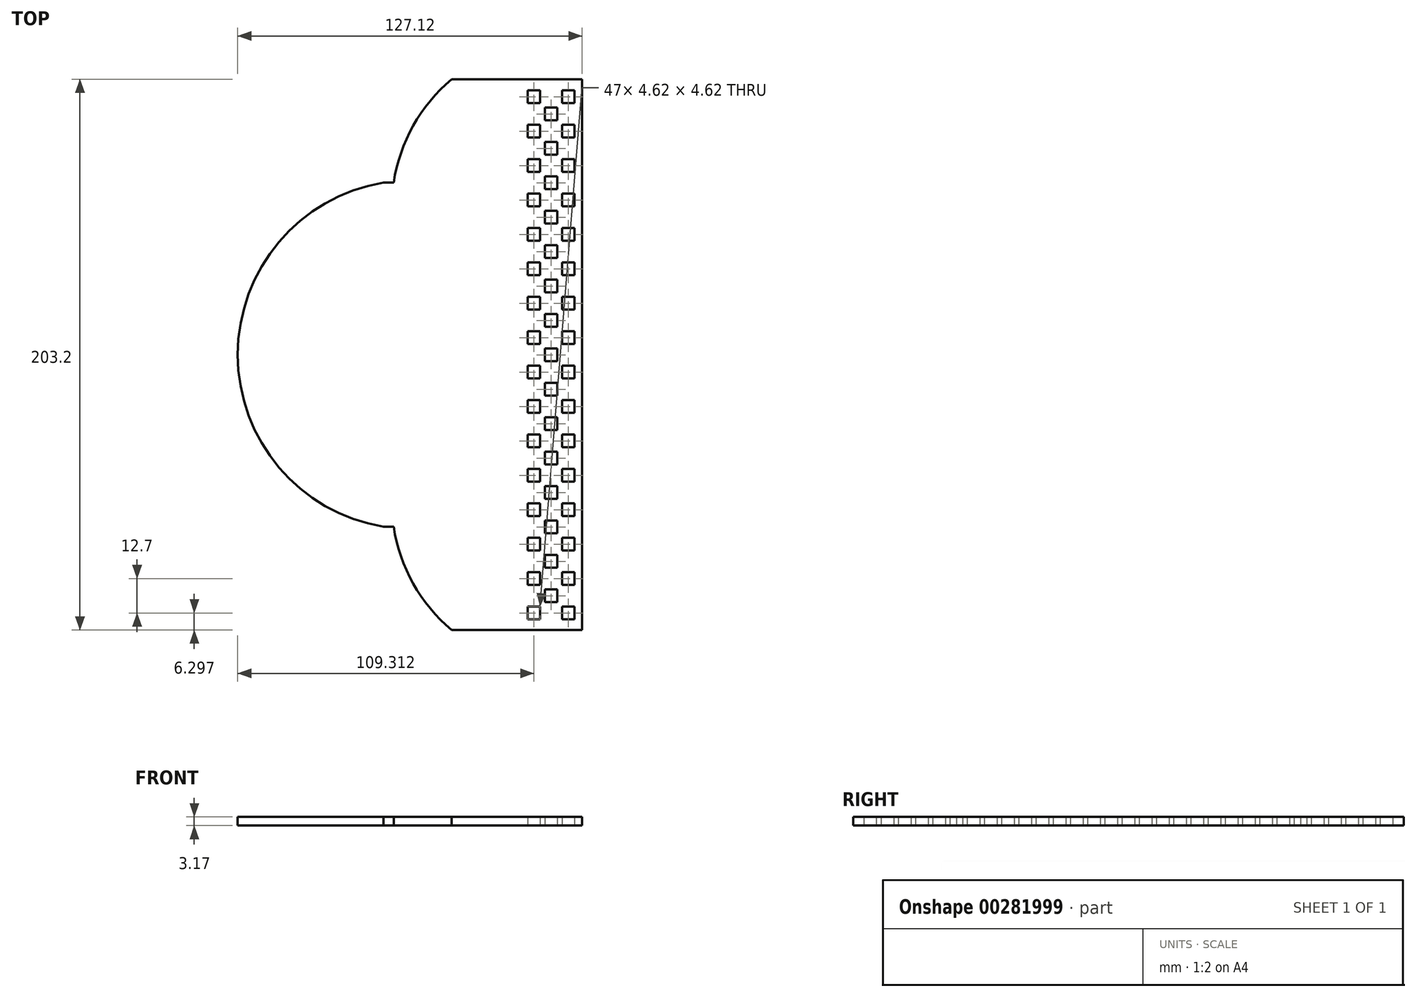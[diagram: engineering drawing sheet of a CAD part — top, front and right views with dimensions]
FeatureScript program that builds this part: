
annotation { "Feature Type Name" : "Feature", "Feature Type Description" : "" }
export const myFeature = defineFeature(function(context is Context, id is Id, definition is map)
    precondition{}
    {
        {
            var Q0;
            Q0=qCreatedBy(makeId("Top.planeOp"),FACE);
            var sketch = newSketch(context, id + "F0", { "sketchPlane" : qUnion([Q0])});
            skLineSegment(sketch, "E0.bottom", {"start": v(-11.58, 137.79) * mm, "end": v(12.55, 137.79) * mm});
            skLineSegment(sketch, "E0.top", {"start": v(-11.58, -65.41) * mm, "end": v(12.55, -65.41) * mm});
            skLineSegment(sketch, "E0.left", {"start": v(-11.58, 137.79) * mm, "end": v(-11.58, -65.41) * mm});
            skLineSegment(sketch, "E0.right", {"start": v(12.55, 137.79) * mm, "end": v(12.55, -65.41) * mm});
            skPoint(sketch, "E1", {"position": v(-7.59, 137.79) * mm});
            skPoint(sketch, "E2", {"position": v(-11.58, 133.7) * mm});
            skLineSegment(sketch, "E3.bottom", {"start": v(-7.59, 133.7) * mm, "end": v(-2.97, 133.7) * mm});
            skLineSegment(sketch, "E3.top", {"start": v(-7.59, 129.08) * mm, "end": v(-2.97, 129.08) * mm});
            skLineSegment(sketch, "E3.left", {"start": v(-7.59, 133.7) * mm, "end": v(-7.59, 129.08) * mm});
            skLineSegment(sketch, "E3.right", {"start": v(-2.97, 133.7) * mm, "end": v(-2.97, 129.08) * mm});
            skPoint(sketch, "E4", {"position": v(-5.28, 133.7) * mm});
            skPoint(sketch, "E5", {"position": v(-7.59, 131.39) * mm});
            skPoint(sketch, "E6", {"position": v(7.42, 133.7) * mm});
            skPoint(sketch, "E7", {"position": v(1.07, 133.7) * mm});
            skLineSegment(sketch, "E8.bottom", {"start": v(5.11, 133.7) * mm, "end": v(9.73, 133.7) * mm});
            skLineSegment(sketch, "E8.top", {"start": v(5.11, 129.08) * mm, "end": v(9.73, 129.08) * mm});
            skLineSegment(sketch, "E8.left", {"start": v(5.11, 133.7) * mm, "end": v(5.11, 129.08) * mm});
            skLineSegment(sketch, "E8.right", {"start": v(9.73, 133.7) * mm, "end": v(9.73, 129.08) * mm});
            skPoint(sketch, "E9", {"position": v(-7.59, 118.84) * mm});
            skPoint(sketch, "E10.0.1.0", {"position": v(7.42, 121) * mm});
            skPoint(sketch, "E10.0.1.1", {"position": v(-7.59, 118.69) * mm});
            skLineSegment(sketch, "E10.0.1.2", {"start": v(9.73, 121) * mm, "end": v(9.73, 116.38) * mm});
            skLineSegment(sketch, "E10.0.1.3", {"start": v(5.11, 121) * mm, "end": v(5.11, 116.38) * mm});
            skLineSegment(sketch, "E10.0.1.4", {"start": v(5.11, 116.38) * mm, "end": v(9.73, 116.38) * mm});
            skLineSegment(sketch, "E10.0.1.5", {"start": v(-2.97, 121) * mm, "end": v(-2.97, 116.38) * mm});
            skLineSegment(sketch, "E10.0.1.6", {"start": v(-7.59, 116.38) * mm, "end": v(-2.97, 116.38) * mm});
            skPoint(sketch, "E10.0.1.7", {"position": v(1.07, 121) * mm});
            skPoint(sketch, "E10.0.1.8", {"position": v(-5.28, 121) * mm});
            skLineSegment(sketch, "E10.0.1.9", {"start": v(5.11, 121) * mm, "end": v(9.73, 121) * mm});
            skLineSegment(sketch, "E10.0.1.10", {"start": v(-7.59, 121) * mm, "end": v(-7.59, 116.38) * mm});
            skLineSegment(sketch, "E10.0.1.11", {"start": v(-7.59, 121) * mm, "end": v(-2.97, 121) * mm});
            skPoint(sketch, "E10.0.2.0", {"position": v(7.42, 108.3) * mm});
            skPoint(sketch, "E10.0.2.1", {"position": v(-7.59, 105.99) * mm});
            skLineSegment(sketch, "E10.0.2.2", {"start": v(9.73, 108.3) * mm, "end": v(9.73, 103.68) * mm});
            skLineSegment(sketch, "E10.0.2.3", {"start": v(5.11, 108.3) * mm, "end": v(5.11, 103.68) * mm});
            skLineSegment(sketch, "E10.0.2.4", {"start": v(5.11, 103.68) * mm, "end": v(9.73, 103.68) * mm});
            skLineSegment(sketch, "E10.0.2.5", {"start": v(-2.97, 108.3) * mm, "end": v(-2.97, 103.68) * mm});
            skLineSegment(sketch, "E10.0.2.6", {"start": v(-7.59, 103.68) * mm, "end": v(-2.97, 103.68) * mm});
            skPoint(sketch, "E10.0.2.7", {"position": v(1.07, 108.3) * mm});
            skPoint(sketch, "E10.0.2.8", {"position": v(-5.28, 108.3) * mm});
            skLineSegment(sketch, "E10.0.2.9", {"start": v(5.11, 108.3) * mm, "end": v(9.73, 108.3) * mm});
            skLineSegment(sketch, "E10.0.2.10", {"start": v(-7.59, 108.3) * mm, "end": v(-7.59, 103.68) * mm});
            skLineSegment(sketch, "E10.0.2.11", {"start": v(-7.59, 108.3) * mm, "end": v(-2.97, 108.3) * mm});
            skPoint(sketch, "E10.0.3.0", {"position": v(7.42, 95.6) * mm});
            skPoint(sketch, "E10.0.3.1", {"position": v(-7.59, 93.29) * mm});
            skLineSegment(sketch, "E10.0.3.2", {"start": v(9.73, 95.6) * mm, "end": v(9.73, 90.98) * mm});
            skLineSegment(sketch, "E10.0.3.3", {"start": v(5.11, 95.6) * mm, "end": v(5.11, 90.98) * mm});
            skLineSegment(sketch, "E10.0.3.4", {"start": v(5.11, 90.98) * mm, "end": v(9.73, 90.98) * mm});
            skLineSegment(sketch, "E10.0.3.5", {"start": v(-2.97, 95.6) * mm, "end": v(-2.97, 90.98) * mm});
            skLineSegment(sketch, "E10.0.3.6", {"start": v(-7.59, 90.98) * mm, "end": v(-2.97, 90.98) * mm});
            skPoint(sketch, "E10.0.3.7", {"position": v(1.07, 95.6) * mm});
            skPoint(sketch, "E10.0.3.8", {"position": v(-5.28, 95.6) * mm});
            skLineSegment(sketch, "E10.0.3.9", {"start": v(5.11, 95.6) * mm, "end": v(9.73, 95.6) * mm});
            skLineSegment(sketch, "E10.0.3.10", {"start": v(-7.59, 95.6) * mm, "end": v(-7.59, 90.98) * mm});
            skLineSegment(sketch, "E10.0.3.11", {"start": v(-7.59, 95.6) * mm, "end": v(-2.97, 95.6) * mm});
            skPoint(sketch, "E10.0.4.0", {"position": v(7.42, 82.9) * mm});
            skPoint(sketch, "E10.0.4.1", {"position": v(-7.59, 80.59) * mm});
            skLineSegment(sketch, "E10.0.4.2", {"start": v(9.73, 82.9) * mm, "end": v(9.73, 78.28) * mm});
            skLineSegment(sketch, "E10.0.4.3", {"start": v(5.11, 82.9) * mm, "end": v(5.11, 78.28) * mm});
            skLineSegment(sketch, "E10.0.4.4", {"start": v(5.11, 78.28) * mm, "end": v(9.73, 78.28) * mm});
            skLineSegment(sketch, "E10.0.4.5", {"start": v(-2.97, 82.9) * mm, "end": v(-2.97, 78.28) * mm});
            skLineSegment(sketch, "E10.0.4.6", {"start": v(-7.59, 78.28) * mm, "end": v(-2.97, 78.28) * mm});
            skPoint(sketch, "E10.0.4.7", {"position": v(1.07, 82.9) * mm});
            skPoint(sketch, "E10.0.4.8", {"position": v(-5.28, 82.9) * mm});
            skLineSegment(sketch, "E10.0.4.9", {"start": v(5.11, 82.9) * mm, "end": v(9.73, 82.9) * mm});
            skLineSegment(sketch, "E10.0.4.10", {"start": v(-7.59, 82.9) * mm, "end": v(-7.59, 78.28) * mm});
            skLineSegment(sketch, "E10.0.4.11", {"start": v(-7.59, 82.9) * mm, "end": v(-2.97, 82.9) * mm});
            skPoint(sketch, "E10.0.5.0", {"position": v(7.42, 70.2) * mm});
            skPoint(sketch, "E10.0.5.1", {"position": v(-7.59, 67.89) * mm});
            skLineSegment(sketch, "E10.0.5.2", {"start": v(9.73, 70.2) * mm, "end": v(9.73, 65.58) * mm});
            skLineSegment(sketch, "E10.0.5.3", {"start": v(5.11, 70.2) * mm, "end": v(5.11, 65.58) * mm});
            skLineSegment(sketch, "E10.0.5.4", {"start": v(5.11, 65.58) * mm, "end": v(9.73, 65.58) * mm});
            skLineSegment(sketch, "E10.0.5.5", {"start": v(-2.97, 70.2) * mm, "end": v(-2.97, 65.58) * mm});
            skLineSegment(sketch, "E10.0.5.6", {"start": v(-7.59, 65.58) * mm, "end": v(-2.97, 65.58) * mm});
            skPoint(sketch, "E10.0.5.7", {"position": v(1.07, 70.2) * mm});
            skPoint(sketch, "E10.0.5.8", {"position": v(-5.28, 70.2) * mm});
            skLineSegment(sketch, "E10.0.5.9", {"start": v(5.11, 70.2) * mm, "end": v(9.73, 70.2) * mm});
            skLineSegment(sketch, "E10.0.5.10", {"start": v(-7.59, 70.2) * mm, "end": v(-7.59, 65.58) * mm});
            skLineSegment(sketch, "E10.0.5.11", {"start": v(-7.59, 70.2) * mm, "end": v(-2.97, 70.2) * mm});
            skPoint(sketch, "E10.0.6.0", {"position": v(7.42, 57.5) * mm});
            skPoint(sketch, "E10.0.6.1", {"position": v(-7.59, 55.19) * mm});
            skLineSegment(sketch, "E10.0.6.2", {"start": v(9.73, 57.5) * mm, "end": v(9.73, 52.88) * mm});
            skLineSegment(sketch, "E10.0.6.3", {"start": v(5.11, 57.5) * mm, "end": v(5.11, 52.88) * mm});
            skLineSegment(sketch, "E10.0.6.4", {"start": v(5.11, 52.88) * mm, "end": v(9.73, 52.88) * mm});
            skLineSegment(sketch, "E10.0.6.5", {"start": v(-2.97, 57.5) * mm, "end": v(-2.97, 52.88) * mm});
            skLineSegment(sketch, "E10.0.6.6", {"start": v(-7.59, 52.88) * mm, "end": v(-2.97, 52.88) * mm});
            skPoint(sketch, "E10.0.6.7", {"position": v(1.07, 57.5) * mm});
            skPoint(sketch, "E10.0.6.8", {"position": v(-5.28, 57.5) * mm});
            skLineSegment(sketch, "E10.0.6.9", {"start": v(5.11, 57.5) * mm, "end": v(9.73, 57.5) * mm});
            skLineSegment(sketch, "E10.0.6.10", {"start": v(-7.59, 57.5) * mm, "end": v(-7.59, 52.88) * mm});
            skLineSegment(sketch, "E10.0.6.11", {"start": v(-7.59, 57.5) * mm, "end": v(-2.97, 57.5) * mm});
            skPoint(sketch, "E10.0.7.0", {"position": v(7.42, 44.8) * mm});
            skPoint(sketch, "E10.0.7.1", {"position": v(-7.59, 42.49) * mm});
            skLineSegment(sketch, "E10.0.7.2", {"start": v(9.73, 44.8) * mm, "end": v(9.73, 40.18) * mm});
            skLineSegment(sketch, "E10.0.7.3", {"start": v(5.11, 44.8) * mm, "end": v(5.11, 40.18) * mm});
            skLineSegment(sketch, "E10.0.7.4", {"start": v(5.11, 40.18) * mm, "end": v(9.73, 40.18) * mm});
            skLineSegment(sketch, "E10.0.7.5", {"start": v(-2.97, 44.8) * mm, "end": v(-2.97, 40.18) * mm});
            skLineSegment(sketch, "E10.0.7.6", {"start": v(-7.59, 40.18) * mm, "end": v(-2.97, 40.18) * mm});
            skPoint(sketch, "E10.0.7.7", {"position": v(1.07, 44.8) * mm});
            skPoint(sketch, "E10.0.7.8", {"position": v(-5.28, 44.8) * mm});
            skLineSegment(sketch, "E10.0.7.9", {"start": v(5.11, 44.8) * mm, "end": v(9.73, 44.8) * mm});
            skLineSegment(sketch, "E10.0.7.10", {"start": v(-7.59, 44.8) * mm, "end": v(-7.59, 40.18) * mm});
            skLineSegment(sketch, "E10.0.7.11", {"start": v(-7.59, 44.8) * mm, "end": v(-2.97, 44.8) * mm});
            skPoint(sketch, "E10.0.8.0", {"position": v(7.42, 32.1) * mm});
            skPoint(sketch, "E10.0.8.1", {"position": v(-7.59, 29.79) * mm});
            skLineSegment(sketch, "E10.0.8.2", {"start": v(9.73, 32.1) * mm, "end": v(9.73, 27.48) * mm});
            skLineSegment(sketch, "E10.0.8.3", {"start": v(5.11, 32.1) * mm, "end": v(5.11, 27.48) * mm});
            skLineSegment(sketch, "E10.0.8.4", {"start": v(5.11, 27.48) * mm, "end": v(9.73, 27.48) * mm});
            skLineSegment(sketch, "E10.0.8.5", {"start": v(-2.97, 32.1) * mm, "end": v(-2.97, 27.48) * mm});
            skLineSegment(sketch, "E10.0.8.6", {"start": v(-7.59, 27.48) * mm, "end": v(-2.97, 27.48) * mm});
            skPoint(sketch, "E10.0.8.7", {"position": v(1.07, 32.1) * mm});
            skPoint(sketch, "E10.0.8.8", {"position": v(-5.28, 32.1) * mm});
            skLineSegment(sketch, "E10.0.8.9", {"start": v(5.11, 32.1) * mm, "end": v(9.73, 32.1) * mm});
            skLineSegment(sketch, "E10.0.8.10", {"start": v(-7.59, 32.1) * mm, "end": v(-7.59, 27.48) * mm});
            skLineSegment(sketch, "E10.0.8.11", {"start": v(-7.59, 32.1) * mm, "end": v(-2.97, 32.1) * mm});
            skPoint(sketch, "E10.0.9.0", {"position": v(7.42, 19.4) * mm});
            skPoint(sketch, "E10.0.9.1", {"position": v(-7.59, 17.09) * mm});
            skLineSegment(sketch, "E10.0.9.2", {"start": v(9.73, 19.4) * mm, "end": v(9.73, 14.78) * mm});
            skLineSegment(sketch, "E10.0.9.3", {"start": v(5.11, 19.4) * mm, "end": v(5.11, 14.78) * mm});
            skLineSegment(sketch, "E10.0.9.4", {"start": v(5.11, 14.78) * mm, "end": v(9.73, 14.78) * mm});
            skLineSegment(sketch, "E10.0.9.5", {"start": v(-2.97, 19.4) * mm, "end": v(-2.97, 14.78) * mm});
            skLineSegment(sketch, "E10.0.9.6", {"start": v(-7.59, 14.78) * mm, "end": v(-2.97, 14.78) * mm});
            skPoint(sketch, "E10.0.9.7", {"position": v(1.07, 19.4) * mm});
            skPoint(sketch, "E10.0.9.8", {"position": v(-5.28, 19.4) * mm});
            skLineSegment(sketch, "E10.0.9.9", {"start": v(5.11, 19.4) * mm, "end": v(9.73, 19.4) * mm});
            skLineSegment(sketch, "E10.0.9.10", {"start": v(-7.59, 19.4) * mm, "end": v(-7.59, 14.78) * mm});
            skLineSegment(sketch, "E10.0.9.11", {"start": v(-7.59, 19.4) * mm, "end": v(-2.97, 19.4) * mm});
            skPoint(sketch, "E10.0.10.0", {"position": v(7.42, 6.7) * mm});
            skPoint(sketch, "E10.0.10.1", {"position": v(-7.59, 4.39) * mm});
            skLineSegment(sketch, "E10.0.10.2", {"start": v(9.73, 6.7) * mm, "end": v(9.73, 2.08) * mm});
            skLineSegment(sketch, "E10.0.10.3", {"start": v(5.11, 6.7) * mm, "end": v(5.11, 2.08) * mm});
            skLineSegment(sketch, "E10.0.10.4", {"start": v(5.11, 2.08) * mm, "end": v(9.73, 2.08) * mm});
            skLineSegment(sketch, "E10.0.10.5", {"start": v(-2.97, 6.7) * mm, "end": v(-2.97, 2.08) * mm});
            skLineSegment(sketch, "E10.0.10.6", {"start": v(-7.59, 2.08) * mm, "end": v(-2.97, 2.08) * mm});
            skPoint(sketch, "E10.0.10.7", {"position": v(1.07, 6.7) * mm});
            skPoint(sketch, "E10.0.10.8", {"position": v(-5.28, 6.7) * mm});
            skLineSegment(sketch, "E10.0.10.9", {"start": v(5.11, 6.7) * mm, "end": v(9.73, 6.7) * mm});
            skLineSegment(sketch, "E10.0.10.10", {"start": v(-7.59, 6.7) * mm, "end": v(-7.59, 2.08) * mm});
            skLineSegment(sketch, "E10.0.10.11", {"start": v(-7.59, 6.7) * mm, "end": v(-2.97, 6.7) * mm});
            skPoint(sketch, "E10.0.11.0", {"position": v(7.42, -6) * mm});
            skPoint(sketch, "E10.0.11.1", {"position": v(-7.59, -8.31) * mm});
            skLineSegment(sketch, "E10.0.11.2", {"start": v(9.73, -6) * mm, "end": v(9.73, -10.62) * mm});
            skLineSegment(sketch, "E10.0.11.3", {"start": v(5.11, -6) * mm, "end": v(5.11, -10.62) * mm});
            skLineSegment(sketch, "E10.0.11.4", {"start": v(5.11, -10.62) * mm, "end": v(9.73, -10.62) * mm});
            skLineSegment(sketch, "E10.0.11.5", {"start": v(-2.97, -6) * mm, "end": v(-2.97, -10.62) * mm});
            skLineSegment(sketch, "E10.0.11.6", {"start": v(-7.59, -10.62) * mm, "end": v(-2.97, -10.62) * mm});
            skPoint(sketch, "E10.0.11.7", {"position": v(1.07, -6) * mm});
            skPoint(sketch, "E10.0.11.8", {"position": v(-5.28, -6) * mm});
            skLineSegment(sketch, "E10.0.11.9", {"start": v(5.11, -6) * mm, "end": v(9.73, -6) * mm});
            skLineSegment(sketch, "E10.0.11.10", {"start": v(-7.59, -6) * mm, "end": v(-7.59, -10.62) * mm});
            skLineSegment(sketch, "E10.0.11.11", {"start": v(-7.59, -6) * mm, "end": v(-2.97, -6) * mm});
            skPoint(sketch, "E10.0.12.0", {"position": v(7.42, -18.7) * mm});
            skPoint(sketch, "E10.0.12.1", {"position": v(-7.59, -21.01) * mm});
            skLineSegment(sketch, "E10.0.12.2", {"start": v(9.73, -18.7) * mm, "end": v(9.73, -23.32) * mm});
            skLineSegment(sketch, "E10.0.12.3", {"start": v(5.11, -18.7) * mm, "end": v(5.11, -23.32) * mm});
            skLineSegment(sketch, "E10.0.12.4", {"start": v(5.11, -23.32) * mm, "end": v(9.73, -23.32) * mm});
            skLineSegment(sketch, "E10.0.12.5", {"start": v(-2.97, -18.7) * mm, "end": v(-2.97, -23.32) * mm});
            skLineSegment(sketch, "E10.0.12.6", {"start": v(-7.59, -23.32) * mm, "end": v(-2.97, -23.32) * mm});
            skPoint(sketch, "E10.0.12.7", {"position": v(1.07, -18.7) * mm});
            skPoint(sketch, "E10.0.12.8", {"position": v(-5.28, -18.7) * mm});
            skLineSegment(sketch, "E10.0.12.9", {"start": v(5.11, -18.7) * mm, "end": v(9.73, -18.7) * mm});
            skLineSegment(sketch, "E10.0.12.10", {"start": v(-7.59, -18.7) * mm, "end": v(-7.59, -23.32) * mm});
            skLineSegment(sketch, "E10.0.12.11", {"start": v(-7.59, -18.7) * mm, "end": v(-2.97, -18.7) * mm});
            skPoint(sketch, "E10.0.13.0", {"position": v(7.42, -31.4) * mm});
            skPoint(sketch, "E10.0.13.1", {"position": v(-7.59, -33.71) * mm});
            skLineSegment(sketch, "E10.0.13.2", {"start": v(9.73, -31.4) * mm, "end": v(9.73, -36.02) * mm});
            skLineSegment(sketch, "E10.0.13.3", {"start": v(5.11, -31.4) * mm, "end": v(5.11, -36.02) * mm});
            skLineSegment(sketch, "E10.0.13.4", {"start": v(5.11, -36.02) * mm, "end": v(9.73, -36.02) * mm});
            skLineSegment(sketch, "E10.0.13.5", {"start": v(-2.97, -31.4) * mm, "end": v(-2.97, -36.02) * mm});
            skLineSegment(sketch, "E10.0.13.6", {"start": v(-7.59, -36.02) * mm, "end": v(-2.97, -36.02) * mm});
            skPoint(sketch, "E10.0.13.7", {"position": v(1.07, -31.4) * mm});
            skPoint(sketch, "E10.0.13.8", {"position": v(-5.28, -31.4) * mm});
            skLineSegment(sketch, "E10.0.13.9", {"start": v(5.11, -31.4) * mm, "end": v(9.73, -31.4) * mm});
            skLineSegment(sketch, "E10.0.13.10", {"start": v(-7.59, -31.4) * mm, "end": v(-7.59, -36.02) * mm});
            skLineSegment(sketch, "E10.0.13.11", {"start": v(-7.59, -31.4) * mm, "end": v(-2.97, -31.4) * mm});
            skPoint(sketch, "E10.0.14.0", {"position": v(7.42, -44.1) * mm});
            skPoint(sketch, "E10.0.14.1", {"position": v(-7.59, -46.41) * mm});
            skLineSegment(sketch, "E10.0.14.2", {"start": v(9.73, -44.1) * mm, "end": v(9.73, -48.72) * mm});
            skLineSegment(sketch, "E10.0.14.3", {"start": v(5.11, -44.1) * mm, "end": v(5.11, -48.72) * mm});
            skLineSegment(sketch, "E10.0.14.4", {"start": v(5.11, -48.72) * mm, "end": v(9.73, -48.72) * mm});
            skLineSegment(sketch, "E10.0.14.5", {"start": v(-2.97, -44.1) * mm, "end": v(-2.97, -48.72) * mm});
            skLineSegment(sketch, "E10.0.14.6", {"start": v(-7.59, -48.72) * mm, "end": v(-2.97, -48.72) * mm});
            skPoint(sketch, "E10.0.14.7", {"position": v(1.07, -44.1) * mm});
            skPoint(sketch, "E10.0.14.8", {"position": v(-5.28, -44.1) * mm});
            skLineSegment(sketch, "E10.0.14.9", {"start": v(5.11, -44.1) * mm, "end": v(9.73, -44.1) * mm});
            skLineSegment(sketch, "E10.0.14.10", {"start": v(-7.59, -44.1) * mm, "end": v(-7.59, -48.72) * mm});
            skLineSegment(sketch, "E10.0.14.11", {"start": v(-7.59, -44.1) * mm, "end": v(-2.97, -44.1) * mm});
            skPoint(sketch, "E10.0.15.0", {"position": v(7.42, -56.8) * mm});
            skPoint(sketch, "E10.0.15.1", {"position": v(-7.59, -59.11) * mm});
            skLineSegment(sketch, "E10.0.15.2", {"start": v(9.73, -56.8) * mm, "end": v(9.73, -61.42) * mm});
            skLineSegment(sketch, "E10.0.15.3", {"start": v(5.11, -56.8) * mm, "end": v(5.11, -61.42) * mm});
            skLineSegment(sketch, "E10.0.15.4", {"start": v(5.11, -61.42) * mm, "end": v(9.73, -61.42) * mm});
            skLineSegment(sketch, "E10.0.15.5", {"start": v(-2.97, -56.8) * mm, "end": v(-2.97, -61.42) * mm});
            skLineSegment(sketch, "E10.0.15.6", {"start": v(-7.59, -61.42) * mm, "end": v(-2.97, -61.42) * mm});
            skPoint(sketch, "E10.0.15.7", {"position": v(1.07, -56.8) * mm});
            skPoint(sketch, "E10.0.15.8", {"position": v(-5.28, -56.8) * mm});
            skLineSegment(sketch, "E10.0.15.9", {"start": v(5.11, -56.8) * mm, "end": v(9.73, -56.8) * mm});
            skLineSegment(sketch, "E10.0.15.10", {"start": v(-7.59, -56.8) * mm, "end": v(-7.59, -61.42) * mm});
            skLineSegment(sketch, "E10.0.15.11", {"start": v(-7.59, -56.8) * mm, "end": v(-2.97, -56.8) * mm});
            skLineSegment(sketch, "E10.direction1", {"start": v(-7.59, 131.39) * mm, "end": v(17.81, 131.39) * mm, "construction": true});
            skLineSegment(sketch, "E10.direction2", {"start": v(-7.59, 131.39) * mm, "end": v(-7.59, 118.69) * mm, "construction": true});
            skPoint(sketch, "E11", {"position": v(1.07, 127.35) * mm});
            skLineSegment(sketch, "E12.bottom", {"start": v(-1.24, 127.35) * mm, "end": v(3.38, 127.35) * mm});
            skLineSegment(sketch, "E12.top", {"start": v(-1.24, 122.73) * mm, "end": v(3.38, 122.73) * mm});
            skLineSegment(sketch, "E12.left", {"start": v(-1.24, 127.35) * mm, "end": v(-1.24, 122.73) * mm});
            skLineSegment(sketch, "E12.right", {"start": v(3.38, 127.35) * mm, "end": v(3.38, 122.73) * mm});
            skLineSegment(sketch, "E13.0.1.0", {"start": v(3.38, 114.65) * mm, "end": v(3.38, 110.03) * mm});
            skLineSegment(sketch, "E13.0.1.1", {"start": v(-1.24, 114.65) * mm, "end": v(-1.24, 110.03) * mm});
            skLineSegment(sketch, "E13.0.1.2", {"start": v(-1.24, 110.03) * mm, "end": v(3.38, 110.03) * mm});
            skPoint(sketch, "E13.0.1.3", {"position": v(1.07, 114.65) * mm});
            skLineSegment(sketch, "E13.0.1.4", {"start": v(-1.24, 114.65) * mm, "end": v(3.38, 114.65) * mm});
            skLineSegment(sketch, "E13.0.2.0", {"start": v(3.38, 101.95) * mm, "end": v(3.38, 97.33) * mm});
            skLineSegment(sketch, "E13.0.2.1", {"start": v(-1.24, 101.95) * mm, "end": v(-1.24, 97.33) * mm});
            skLineSegment(sketch, "E13.0.2.2", {"start": v(-1.24, 97.33) * mm, "end": v(3.38, 97.33) * mm});
            skPoint(sketch, "E13.0.2.3", {"position": v(1.07, 101.95) * mm});
            skLineSegment(sketch, "E13.0.2.4", {"start": v(-1.24, 101.95) * mm, "end": v(3.38, 101.95) * mm});
            skLineSegment(sketch, "E13.0.3.0", {"start": v(3.38, 89.25) * mm, "end": v(3.38, 84.63) * mm});
            skLineSegment(sketch, "E13.0.3.1", {"start": v(-1.24, 89.25) * mm, "end": v(-1.24, 84.63) * mm});
            skLineSegment(sketch, "E13.0.3.2", {"start": v(-1.24, 84.63) * mm, "end": v(3.38, 84.63) * mm});
            skPoint(sketch, "E13.0.3.3", {"position": v(1.07, 89.25) * mm});
            skLineSegment(sketch, "E13.0.3.4", {"start": v(-1.24, 89.25) * mm, "end": v(3.38, 89.25) * mm});
            skLineSegment(sketch, "E13.0.4.0", {"start": v(3.38, 76.55) * mm, "end": v(3.38, 71.93) * mm});
            skLineSegment(sketch, "E13.0.4.1", {"start": v(-1.24, 76.55) * mm, "end": v(-1.24, 71.93) * mm});
            skLineSegment(sketch, "E13.0.4.2", {"start": v(-1.24, 71.93) * mm, "end": v(3.38, 71.93) * mm});
            skPoint(sketch, "E13.0.4.3", {"position": v(1.07, 76.55) * mm});
            skLineSegment(sketch, "E13.0.4.4", {"start": v(-1.24, 76.55) * mm, "end": v(3.38, 76.55) * mm});
            skLineSegment(sketch, "E13.0.5.0", {"start": v(3.38, 63.85) * mm, "end": v(3.38, 59.23) * mm});
            skLineSegment(sketch, "E13.0.5.1", {"start": v(-1.24, 63.85) * mm, "end": v(-1.24, 59.23) * mm});
            skLineSegment(sketch, "E13.0.5.2", {"start": v(-1.24, 59.23) * mm, "end": v(3.38, 59.23) * mm});
            skPoint(sketch, "E13.0.5.3", {"position": v(1.07, 63.85) * mm});
            skLineSegment(sketch, "E13.0.5.4", {"start": v(-1.24, 63.85) * mm, "end": v(3.38, 63.85) * mm});
            skLineSegment(sketch, "E13.0.6.0", {"start": v(3.38, 51.15) * mm, "end": v(3.38, 46.53) * mm});
            skLineSegment(sketch, "E13.0.6.1", {"start": v(-1.24, 51.15) * mm, "end": v(-1.24, 46.53) * mm});
            skLineSegment(sketch, "E13.0.6.2", {"start": v(-1.24, 46.53) * mm, "end": v(3.38, 46.53) * mm});
            skPoint(sketch, "E13.0.6.3", {"position": v(1.07, 51.15) * mm});
            skLineSegment(sketch, "E13.0.6.4", {"start": v(-1.24, 51.15) * mm, "end": v(3.38, 51.15) * mm});
            skLineSegment(sketch, "E13.0.7.0", {"start": v(3.38, 38.45) * mm, "end": v(3.38, 33.83) * mm});
            skLineSegment(sketch, "E13.0.7.1", {"start": v(-1.24, 38.45) * mm, "end": v(-1.24, 33.83) * mm});
            skLineSegment(sketch, "E13.0.7.2", {"start": v(-1.24, 33.83) * mm, "end": v(3.38, 33.83) * mm});
            skPoint(sketch, "E13.0.7.3", {"position": v(1.07, 38.45) * mm});
            skLineSegment(sketch, "E13.0.7.4", {"start": v(-1.24, 38.45) * mm, "end": v(3.38, 38.45) * mm});
            skLineSegment(sketch, "E13.0.8.0", {"start": v(3.38, 25.75) * mm, "end": v(3.38, 21.13) * mm});
            skLineSegment(sketch, "E13.0.8.1", {"start": v(-1.24, 25.75) * mm, "end": v(-1.24, 21.13) * mm});
            skLineSegment(sketch, "E13.0.8.2", {"start": v(-1.24, 21.13) * mm, "end": v(3.38, 21.13) * mm});
            skPoint(sketch, "E13.0.8.3", {"position": v(1.07, 25.75) * mm});
            skLineSegment(sketch, "E13.0.8.4", {"start": v(-1.24, 25.75) * mm, "end": v(3.38, 25.75) * mm});
            skLineSegment(sketch, "E13.0.9.0", {"start": v(3.38, 13.05) * mm, "end": v(3.38, 8.43) * mm});
            skLineSegment(sketch, "E13.0.9.1", {"start": v(-1.24, 13.05) * mm, "end": v(-1.24, 8.43) * mm});
            skLineSegment(sketch, "E13.0.9.2", {"start": v(-1.24, 8.43) * mm, "end": v(3.38, 8.43) * mm});
            skPoint(sketch, "E13.0.9.3", {"position": v(1.07, 13.05) * mm});
            skLineSegment(sketch, "E13.0.9.4", {"start": v(-1.24, 13.05) * mm, "end": v(3.38, 13.05) * mm});
            skLineSegment(sketch, "E13.0.10.0", {"start": v(3.38, 0.35) * mm, "end": v(3.38, -4.27) * mm});
            skLineSegment(sketch, "E13.0.10.1", {"start": v(-1.24, 0.35) * mm, "end": v(-1.24, -4.27) * mm});
            skLineSegment(sketch, "E13.0.10.2", {"start": v(-1.24, -4.27) * mm, "end": v(3.38, -4.27) * mm});
            skPoint(sketch, "E13.0.10.3", {"position": v(1.07, 0.35) * mm});
            skLineSegment(sketch, "E13.0.10.4", {"start": v(-1.24, 0.35) * mm, "end": v(3.38, 0.35) * mm});
            skLineSegment(sketch, "E13.0.11.0", {"start": v(3.38, -12.35) * mm, "end": v(3.38, -16.97) * mm});
            skLineSegment(sketch, "E13.0.11.1", {"start": v(-1.24, -12.35) * mm, "end": v(-1.24, -16.97) * mm});
            skLineSegment(sketch, "E13.0.11.2", {"start": v(-1.24, -16.97) * mm, "end": v(3.38, -16.97) * mm});
            skPoint(sketch, "E13.0.11.3", {"position": v(1.07, -12.35) * mm});
            skLineSegment(sketch, "E13.0.11.4", {"start": v(-1.24, -12.35) * mm, "end": v(3.38, -12.35) * mm});
            skLineSegment(sketch, "E13.0.12.0", {"start": v(3.38, -25.05) * mm, "end": v(3.38, -29.67) * mm});
            skLineSegment(sketch, "E13.0.12.1", {"start": v(-1.24, -25.05) * mm, "end": v(-1.24, -29.67) * mm});
            skLineSegment(sketch, "E13.0.12.2", {"start": v(-1.24, -29.67) * mm, "end": v(3.38, -29.67) * mm});
            skPoint(sketch, "E13.0.12.3", {"position": v(1.07, -25.05) * mm});
            skLineSegment(sketch, "E13.0.12.4", {"start": v(-1.24, -25.05) * mm, "end": v(3.38, -25.05) * mm});
            skLineSegment(sketch, "E13.0.13.0", {"start": v(3.38, -37.75) * mm, "end": v(3.38, -42.37) * mm});
            skLineSegment(sketch, "E13.0.13.1", {"start": v(-1.24, -37.75) * mm, "end": v(-1.24, -42.37) * mm});
            skLineSegment(sketch, "E13.0.13.2", {"start": v(-1.24, -42.37) * mm, "end": v(3.38, -42.37) * mm});
            skPoint(sketch, "E13.0.13.3", {"position": v(1.07, -37.75) * mm});
            skLineSegment(sketch, "E13.0.13.4", {"start": v(-1.24, -37.75) * mm, "end": v(3.38, -37.75) * mm});
            skLineSegment(sketch, "E13.0.14.0", {"start": v(3.38, -50.45) * mm, "end": v(3.38, -55.07) * mm});
            skLineSegment(sketch, "E13.0.14.1", {"start": v(-1.24, -50.45) * mm, "end": v(-1.24, -55.07) * mm});
            skLineSegment(sketch, "E13.0.14.2", {"start": v(-1.24, -55.07) * mm, "end": v(3.38, -55.07) * mm});
            skPoint(sketch, "E13.0.14.3", {"position": v(1.07, -50.45) * mm});
            skLineSegment(sketch, "E13.0.14.4", {"start": v(-1.24, -50.45) * mm, "end": v(3.38, -50.45) * mm});
            skLineSegment(sketch, "E13.direction1", {"start": v(-1.24, 122.73) * mm, "end": v(24.16, 122.73) * mm, "construction": true});
            skLineSegment(sketch, "E13.direction2", {"start": v(-1.24, 122.73) * mm, "end": v(-1.24, 110.03) * mm, "construction": true});
            skSolve(sketch);
        }
        {
            var Q0;
            Q0=makeQuery(id+"F0.imprint","IMPRINT",FACE,{"disambiguationData":[TD([[makeQuery(id+"F0.imprint","IMPRINT",EDGE,{"derivedFrom":sQuery(id+"F0.wireOp",EDGE,"E0.bottom")}),-1.0]])]});
            extrude(context, id + "F1", {"entities" : qUnion([Q0]), "depth" : 3.17 * mm});
        }
        {
            var Q0;
            Q0=makeQuery(id+"F1.opExtrude","SWEPT_BODY",BODY,{"disambiguationData":[OSD([sQuery(id+"F0.wireOp",EDGE,"E0.bottom"),sQuery(id+"F0.wireOp",EDGE,"E0.top"),sQuery(id+"F0.wireOp",EDGE,"E0.left"),sQuery(id+"F0.wireOp",EDGE,"E0.right"),sQuery(id+"F0.wireOp",EDGE,"E3.bottom"),sQuery(id+"F0.wireOp",EDGE,"E3.top"),sQuery(id+"F0.wireOp",EDGE,"E3.left"),sQuery(id+"F0.wireOp",EDGE,"E3.right"),sQuery(id+"F0.wireOp",EDGE,"E8.bottom"),sQuery(id+"F0.wireOp",EDGE,"E8.top"),sQuery(id+"F0.wireOp",EDGE,"E8.left"),sQuery(id+"F0.wireOp",EDGE,"E8.right"),sQuery(id+"F0.wireOp",EDGE,"E10.0.1.2"),sQuery(id+"F0.wireOp",EDGE,"E10.0.1.3"),sQuery(id+"F0.wireOp",EDGE,"E10.0.1.4"),sQuery(id+"F0.wireOp",EDGE,"E10.0.1.5"),sQuery(id+"F0.wireOp",EDGE,"E10.0.1.6"),sQuery(id+"F0.wireOp",EDGE,"E10.0.1.9"),sQuery(id+"F0.wireOp",EDGE,"E10.0.1.10"),sQuery(id+"F0.wireOp",EDGE,"E10.0.1.11"),sQuery(id+"F0.wireOp",EDGE,"E10.0.2.2"),sQuery(id+"F0.wireOp",EDGE,"E10.0.2.3"),sQuery(id+"F0.wireOp",EDGE,"E10.0.2.4"),sQuery(id+"F0.wireOp",EDGE,"E10.0.2.5"),sQuery(id+"F0.wireOp",EDGE,"E10.0.2.6"),sQuery(id+"F0.wireOp",EDGE,"E10.0.2.9"),sQuery(id+"F0.wireOp",EDGE,"E10.0.2.10"),sQuery(id+"F0.wireOp",EDGE,"E10.0.2.11"),sQuery(id+"F0.wireOp",EDGE,"E10.0.3.2"),sQuery(id+"F0.wireOp",EDGE,"E10.0.3.3"),sQuery(id+"F0.wireOp",EDGE,"E10.0.3.4"),sQuery(id+"F0.wireOp",EDGE,"E10.0.3.5"),sQuery(id+"F0.wireOp",EDGE,"E10.0.3.6"),sQuery(id+"F0.wireOp",EDGE,"E10.0.3.9"),sQuery(id+"F0.wireOp",EDGE,"E10.0.3.10"),sQuery(id+"F0.wireOp",EDGE,"E10.0.3.11"),sQuery(id+"F0.wireOp",EDGE,"E10.0.4.2"),sQuery(id+"F0.wireOp",EDGE,"E10.0.4.3"),sQuery(id+"F0.wireOp",EDGE,"E10.0.4.4"),sQuery(id+"F0.wireOp",EDGE,"E10.0.4.5"),sQuery(id+"F0.wireOp",EDGE,"E10.0.4.6"),sQuery(id+"F0.wireOp",EDGE,"E10.0.4.9"),sQuery(id+"F0.wireOp",EDGE,"E10.0.4.10"),sQuery(id+"F0.wireOp",EDGE,"E10.0.4.11"),sQuery(id+"F0.wireOp",EDGE,"E10.0.5.2"),sQuery(id+"F0.wireOp",EDGE,"E10.0.5.3"),sQuery(id+"F0.wireOp",EDGE,"E10.0.5.4"),sQuery(id+"F0.wireOp",EDGE,"E10.0.5.5"),sQuery(id+"F0.wireOp",EDGE,"E10.0.5.6"),sQuery(id+"F0.wireOp",EDGE,"E10.0.5.9"),sQuery(id+"F0.wireOp",EDGE,"E10.0.5.10"),sQuery(id+"F0.wireOp",EDGE,"E10.0.5.11"),sQuery(id+"F0.wireOp",EDGE,"E10.0.6.2"),sQuery(id+"F0.wireOp",EDGE,"E10.0.6.3"),sQuery(id+"F0.wireOp",EDGE,"E10.0.6.4"),sQuery(id+"F0.wireOp",EDGE,"E10.0.6.5"),sQuery(id+"F0.wireOp",EDGE,"E10.0.6.6"),sQuery(id+"F0.wireOp",EDGE,"E10.0.6.9"),sQuery(id+"F0.wireOp",EDGE,"E10.0.6.10"),sQuery(id+"F0.wireOp",EDGE,"E10.0.6.11"),sQuery(id+"F0.wireOp",EDGE,"E10.0.7.2"),sQuery(id+"F0.wireOp",EDGE,"E10.0.7.3"),sQuery(id+"F0.wireOp",EDGE,"E10.0.7.4"),sQuery(id+"F0.wireOp",EDGE,"E10.0.7.5"),sQuery(id+"F0.wireOp",EDGE,"E10.0.7.6"),sQuery(id+"F0.wireOp",EDGE,"E10.0.7.9"),sQuery(id+"F0.wireOp",EDGE,"E10.0.7.10"),sQuery(id+"F0.wireOp",EDGE,"E10.0.7.11"),sQuery(id+"F0.wireOp",EDGE,"E10.0.8.2"),sQuery(id+"F0.wireOp",EDGE,"E10.0.8.3"),sQuery(id+"F0.wireOp",EDGE,"E10.0.8.4"),sQuery(id+"F0.wireOp",EDGE,"E10.0.8.5"),sQuery(id+"F0.wireOp",EDGE,"E10.0.8.6"),sQuery(id+"F0.wireOp",EDGE,"E10.0.8.9"),sQuery(id+"F0.wireOp",EDGE,"E10.0.8.10"),sQuery(id+"F0.wireOp",EDGE,"E10.0.8.11"),sQuery(id+"F0.wireOp",EDGE,"E10.0.9.2"),sQuery(id+"F0.wireOp",EDGE,"E10.0.9.3"),sQuery(id+"F0.wireOp",EDGE,"E10.0.9.4"),sQuery(id+"F0.wireOp",EDGE,"E10.0.9.5"),sQuery(id+"F0.wireOp",EDGE,"E10.0.9.6"),sQuery(id+"F0.wireOp",EDGE,"E10.0.9.9"),sQuery(id+"F0.wireOp",EDGE,"E10.0.9.10"),sQuery(id+"F0.wireOp",EDGE,"E10.0.9.11"),sQuery(id+"F0.wireOp",EDGE,"E10.0.10.2"),sQuery(id+"F0.wireOp",EDGE,"E10.0.10.3"),sQuery(id+"F0.wireOp",EDGE,"E10.0.10.4"),sQuery(id+"F0.wireOp",EDGE,"E10.0.10.5"),sQuery(id+"F0.wireOp",EDGE,"E10.0.10.6"),sQuery(id+"F0.wireOp",EDGE,"E10.0.10.9"),sQuery(id+"F0.wireOp",EDGE,"E10.0.10.10"),sQuery(id+"F0.wireOp",EDGE,"E10.0.10.11"),sQuery(id+"F0.wireOp",EDGE,"E10.0.11.2"),sQuery(id+"F0.wireOp",EDGE,"E10.0.11.3"),sQuery(id+"F0.wireOp",EDGE,"E10.0.11.4"),sQuery(id+"F0.wireOp",EDGE,"E10.0.11.5"),sQuery(id+"F0.wireOp",EDGE,"E10.0.11.6"),sQuery(id+"F0.wireOp",EDGE,"E10.0.11.9"),sQuery(id+"F0.wireOp",EDGE,"E10.0.11.10"),sQuery(id+"F0.wireOp",EDGE,"E10.0.11.11"),sQuery(id+"F0.wireOp",EDGE,"E10.0.12.2"),sQuery(id+"F0.wireOp",EDGE,"E10.0.12.3"),sQuery(id+"F0.wireOp",EDGE,"E10.0.12.4"),sQuery(id+"F0.wireOp",EDGE,"E10.0.12.5"),sQuery(id+"F0.wireOp",EDGE,"E10.0.12.6"),sQuery(id+"F0.wireOp",EDGE,"E10.0.12.9"),sQuery(id+"F0.wireOp",EDGE,"E10.0.12.10"),sQuery(id+"F0.wireOp",EDGE,"E10.0.12.11"),sQuery(id+"F0.wireOp",EDGE,"E10.0.13.2"),sQuery(id+"F0.wireOp",EDGE,"E10.0.13.3"),sQuery(id+"F0.wireOp",EDGE,"E10.0.13.4"),sQuery(id+"F0.wireOp",EDGE,"E10.0.13.5"),sQuery(id+"F0.wireOp",EDGE,"E10.0.13.6"),sQuery(id+"F0.wireOp",EDGE,"E10.0.13.9"),sQuery(id+"F0.wireOp",EDGE,"E10.0.13.10"),sQuery(id+"F0.wireOp",EDGE,"E10.0.13.11"),sQuery(id+"F0.wireOp",EDGE,"E10.0.14.2"),sQuery(id+"F0.wireOp",EDGE,"E10.0.14.3"),sQuery(id+"F0.wireOp",EDGE,"E10.0.14.4"),sQuery(id+"F0.wireOp",EDGE,"E10.0.14.5"),sQuery(id+"F0.wireOp",EDGE,"E10.0.14.6"),sQuery(id+"F0.wireOp",EDGE,"E10.0.14.9"),sQuery(id+"F0.wireOp",EDGE,"E10.0.14.10"),sQuery(id+"F0.wireOp",EDGE,"E10.0.14.11"),sQuery(id+"F0.wireOp",EDGE,"E10.0.15.2"),sQuery(id+"F0.wireOp",EDGE,"E10.0.15.3"),sQuery(id+"F0.wireOp",EDGE,"E10.0.15.4"),sQuery(id+"F0.wireOp",EDGE,"E10.0.15.5"),sQuery(id+"F0.wireOp",EDGE,"E10.0.15.6"),sQuery(id+"F0.wireOp",EDGE,"E10.0.15.9"),sQuery(id+"F0.wireOp",EDGE,"E10.0.15.10"),sQuery(id+"F0.wireOp",EDGE,"E10.0.15.11"),sQuery(id+"F0.wireOp",EDGE,"E12.bottom"),sQuery(id+"F0.wireOp",EDGE,"E12.top"),sQuery(id+"F0.wireOp",EDGE,"E12.left"),sQuery(id+"F0.wireOp",EDGE,"E12.right"),sQuery(id+"F0.wireOp",EDGE,"E13.0.1.0"),sQuery(id+"F0.wireOp",EDGE,"E13.0.1.1"),sQuery(id+"F0.wireOp",EDGE,"E13.0.1.2"),sQuery(id+"F0.wireOp",EDGE,"E13.0.1.4"),sQuery(id+"F0.wireOp",EDGE,"E13.0.2.0"),sQuery(id+"F0.wireOp",EDGE,"E13.0.2.1"),sQuery(id+"F0.wireOp",EDGE,"E13.0.2.2"),sQuery(id+"F0.wireOp",EDGE,"E13.0.2.4"),sQuery(id+"F0.wireOp",EDGE,"E13.0.3.0"),sQuery(id+"F0.wireOp",EDGE,"E13.0.3.1"),sQuery(id+"F0.wireOp",EDGE,"E13.0.3.2"),sQuery(id+"F0.wireOp",EDGE,"E13.0.3.4"),sQuery(id+"F0.wireOp",EDGE,"E13.0.4.0"),sQuery(id+"F0.wireOp",EDGE,"E13.0.4.1"),sQuery(id+"F0.wireOp",EDGE,"E13.0.4.2"),sQuery(id+"F0.wireOp",EDGE,"E13.0.4.4"),sQuery(id+"F0.wireOp",EDGE,"E13.0.5.0"),sQuery(id+"F0.wireOp",EDGE,"E13.0.5.1"),sQuery(id+"F0.wireOp",EDGE,"E13.0.5.2"),sQuery(id+"F0.wireOp",EDGE,"E13.0.5.4"),sQuery(id+"F0.wireOp",EDGE,"E13.0.6.0"),sQuery(id+"F0.wireOp",EDGE,"E13.0.6.1"),sQuery(id+"F0.wireOp",EDGE,"E13.0.6.2"),sQuery(id+"F0.wireOp",EDGE,"E13.0.6.4"),sQuery(id+"F0.wireOp",EDGE,"E13.0.7.0"),sQuery(id+"F0.wireOp",EDGE,"E13.0.7.1"),sQuery(id+"F0.wireOp",EDGE,"E13.0.7.2"),sQuery(id+"F0.wireOp",EDGE,"E13.0.7.4"),sQuery(id+"F0.wireOp",EDGE,"E13.0.8.0"),sQuery(id+"F0.wireOp",EDGE,"E13.0.8.1"),sQuery(id+"F0.wireOp",EDGE,"E13.0.8.2"),sQuery(id+"F0.wireOp",EDGE,"E13.0.8.4"),sQuery(id+"F0.wireOp",EDGE,"E13.0.9.0"),sQuery(id+"F0.wireOp",EDGE,"E13.0.9.1"),sQuery(id+"F0.wireOp",EDGE,"E13.0.9.2"),sQuery(id+"F0.wireOp",EDGE,"E13.0.9.4"),sQuery(id+"F0.wireOp",EDGE,"E13.0.10.0"),sQuery(id+"F0.wireOp",EDGE,"E13.0.10.1"),sQuery(id+"F0.wireOp",EDGE,"E13.0.10.2"),sQuery(id+"F0.wireOp",EDGE,"E13.0.10.4"),sQuery(id+"F0.wireOp",EDGE,"E13.0.11.0"),sQuery(id+"F0.wireOp",EDGE,"E13.0.11.1"),sQuery(id+"F0.wireOp",EDGE,"E13.0.11.2"),sQuery(id+"F0.wireOp",EDGE,"E13.0.11.4"),sQuery(id+"F0.wireOp",EDGE,"E13.0.12.0"),sQuery(id+"F0.wireOp",EDGE,"E13.0.12.1"),sQuery(id+"F0.wireOp",EDGE,"E13.0.12.2"),sQuery(id+"F0.wireOp",EDGE,"E13.0.12.4"),sQuery(id+"F0.wireOp",EDGE,"E13.0.13.0"),sQuery(id+"F0.wireOp",EDGE,"E13.0.13.1"),sQuery(id+"F0.wireOp",EDGE,"E13.0.13.2"),sQuery(id+"F0.wireOp",EDGE,"E13.0.13.4"),sQuery(id+"F0.wireOp",EDGE,"E13.0.14.0"),sQuery(id+"F0.wireOp",EDGE,"E13.0.14.1"),sQuery(id+"F0.wireOp",EDGE,"E13.0.14.2"),sQuery(id+"F0.wireOp",EDGE,"E13.0.14.4")])]});
            var Q1;
            Q1=makeQuery(id+"F1.opExtrude","SWEPT_FACE",FACE,{"disambiguationData":[OSD([sQuery(id+"F0.wireOp",EDGE,"E0.left")])]});
            mirror(context, id + "F2", {"operationType" : NewBodyOperationType.ADD, "entities" : qUnion([Q0]), "mirrorPlane" : qUnion([Q1])});
        }
        {
            var Q0;
            {var subQ0=makeQuery(id+"F1.opExtrude","CAP_FACE",FACE,{"disambiguationData":[OSD([sQuery(id+"F0.wireOp",EDGE,"E0.bottom"),sQuery(id+"F0.wireOp",EDGE,"E0.top"),sQuery(id+"F0.wireOp",EDGE,"E0.left"),sQuery(id+"F0.wireOp",EDGE,"E0.right"),sQuery(id+"F0.wireOp",EDGE,"E3.bottom"),sQuery(id+"F0.wireOp",EDGE,"E3.top"),sQuery(id+"F0.wireOp",EDGE,"E3.left"),sQuery(id+"F0.wireOp",EDGE,"E3.right"),sQuery(id+"F0.wireOp",EDGE,"E8.bottom"),sQuery(id+"F0.wireOp",EDGE,"E8.top"),sQuery(id+"F0.wireOp",EDGE,"E8.left"),sQuery(id+"F0.wireOp",EDGE,"E8.right"),sQuery(id+"F0.wireOp",EDGE,"E10.0.1.2"),sQuery(id+"F0.wireOp",EDGE,"E10.0.1.3"),sQuery(id+"F0.wireOp",EDGE,"E10.0.1.4"),sQuery(id+"F0.wireOp",EDGE,"E10.0.1.5"),sQuery(id+"F0.wireOp",EDGE,"E10.0.1.6"),sQuery(id+"F0.wireOp",EDGE,"E10.0.1.9"),sQuery(id+"F0.wireOp",EDGE,"E10.0.1.10"),sQuery(id+"F0.wireOp",EDGE,"E10.0.1.11"),sQuery(id+"F0.wireOp",EDGE,"E10.0.2.2"),sQuery(id+"F0.wireOp",EDGE,"E10.0.2.3"),sQuery(id+"F0.wireOp",EDGE,"E10.0.2.4"),sQuery(id+"F0.wireOp",EDGE,"E10.0.2.5"),sQuery(id+"F0.wireOp",EDGE,"E10.0.2.6"),sQuery(id+"F0.wireOp",EDGE,"E10.0.2.9"),sQuery(id+"F0.wireOp",EDGE,"E10.0.2.10"),sQuery(id+"F0.wireOp",EDGE,"E10.0.2.11"),sQuery(id+"F0.wireOp",EDGE,"E10.0.3.2"),sQuery(id+"F0.wireOp",EDGE,"E10.0.3.3"),sQuery(id+"F0.wireOp",EDGE,"E10.0.3.4"),sQuery(id+"F0.wireOp",EDGE,"E10.0.3.5"),sQuery(id+"F0.wireOp",EDGE,"E10.0.3.6"),sQuery(id+"F0.wireOp",EDGE,"E10.0.3.9"),sQuery(id+"F0.wireOp",EDGE,"E10.0.3.10"),sQuery(id+"F0.wireOp",EDGE,"E10.0.3.11"),sQuery(id+"F0.wireOp",EDGE,"E10.0.4.2"),sQuery(id+"F0.wireOp",EDGE,"E10.0.4.3"),sQuery(id+"F0.wireOp",EDGE,"E10.0.4.4"),sQuery(id+"F0.wireOp",EDGE,"E10.0.4.5"),sQuery(id+"F0.wireOp",EDGE,"E10.0.4.6"),sQuery(id+"F0.wireOp",EDGE,"E10.0.4.9"),sQuery(id+"F0.wireOp",EDGE,"E10.0.4.10"),sQuery(id+"F0.wireOp",EDGE,"E10.0.4.11"),sQuery(id+"F0.wireOp",EDGE,"E10.0.5.2"),sQuery(id+"F0.wireOp",EDGE,"E10.0.5.3"),sQuery(id+"F0.wireOp",EDGE,"E10.0.5.4"),sQuery(id+"F0.wireOp",EDGE,"E10.0.5.5"),sQuery(id+"F0.wireOp",EDGE,"E10.0.5.6"),sQuery(id+"F0.wireOp",EDGE,"E10.0.5.9"),sQuery(id+"F0.wireOp",EDGE,"E10.0.5.10"),sQuery(id+"F0.wireOp",EDGE,"E10.0.5.11"),sQuery(id+"F0.wireOp",EDGE,"E10.0.6.2"),sQuery(id+"F0.wireOp",EDGE,"E10.0.6.3"),sQuery(id+"F0.wireOp",EDGE,"E10.0.6.4"),sQuery(id+"F0.wireOp",EDGE,"E10.0.6.5"),sQuery(id+"F0.wireOp",EDGE,"E10.0.6.6"),sQuery(id+"F0.wireOp",EDGE,"E10.0.6.9"),sQuery(id+"F0.wireOp",EDGE,"E10.0.6.10"),sQuery(id+"F0.wireOp",EDGE,"E10.0.6.11"),sQuery(id+"F0.wireOp",EDGE,"E10.0.7.2"),sQuery(id+"F0.wireOp",EDGE,"E10.0.7.3"),sQuery(id+"F0.wireOp",EDGE,"E10.0.7.4"),sQuery(id+"F0.wireOp",EDGE,"E10.0.7.5"),sQuery(id+"F0.wireOp",EDGE,"E10.0.7.6"),sQuery(id+"F0.wireOp",EDGE,"E10.0.7.9"),sQuery(id+"F0.wireOp",EDGE,"E10.0.7.10"),sQuery(id+"F0.wireOp",EDGE,"E10.0.7.11"),sQuery(id+"F0.wireOp",EDGE,"E10.0.8.2"),sQuery(id+"F0.wireOp",EDGE,"E10.0.8.3"),sQuery(id+"F0.wireOp",EDGE,"E10.0.8.4"),sQuery(id+"F0.wireOp",EDGE,"E10.0.8.5"),sQuery(id+"F0.wireOp",EDGE,"E10.0.8.6"),sQuery(id+"F0.wireOp",EDGE,"E10.0.8.9"),sQuery(id+"F0.wireOp",EDGE,"E10.0.8.10"),sQuery(id+"F0.wireOp",EDGE,"E10.0.8.11"),sQuery(id+"F0.wireOp",EDGE,"E10.0.9.2"),sQuery(id+"F0.wireOp",EDGE,"E10.0.9.3"),sQuery(id+"F0.wireOp",EDGE,"E10.0.9.4"),sQuery(id+"F0.wireOp",EDGE,"E10.0.9.5"),sQuery(id+"F0.wireOp",EDGE,"E10.0.9.6"),sQuery(id+"F0.wireOp",EDGE,"E10.0.9.9"),sQuery(id+"F0.wireOp",EDGE,"E10.0.9.10"),sQuery(id+"F0.wireOp",EDGE,"E10.0.9.11"),sQuery(id+"F0.wireOp",EDGE,"E10.0.10.2"),sQuery(id+"F0.wireOp",EDGE,"E10.0.10.3"),sQuery(id+"F0.wireOp",EDGE,"E10.0.10.4"),sQuery(id+"F0.wireOp",EDGE,"E10.0.10.5"),sQuery(id+"F0.wireOp",EDGE,"E10.0.10.6"),sQuery(id+"F0.wireOp",EDGE,"E10.0.10.9"),sQuery(id+"F0.wireOp",EDGE,"E10.0.10.10"),sQuery(id+"F0.wireOp",EDGE,"E10.0.10.11"),sQuery(id+"F0.wireOp",EDGE,"E10.0.11.2"),sQuery(id+"F0.wireOp",EDGE,"E10.0.11.3"),sQuery(id+"F0.wireOp",EDGE,"E10.0.11.4"),sQuery(id+"F0.wireOp",EDGE,"E10.0.11.5"),sQuery(id+"F0.wireOp",EDGE,"E10.0.11.6"),sQuery(id+"F0.wireOp",EDGE,"E10.0.11.9"),sQuery(id+"F0.wireOp",EDGE,"E10.0.11.10"),sQuery(id+"F0.wireOp",EDGE,"E10.0.11.11"),sQuery(id+"F0.wireOp",EDGE,"E10.0.12.2"),sQuery(id+"F0.wireOp",EDGE,"E10.0.12.3"),sQuery(id+"F0.wireOp",EDGE,"E10.0.12.4"),sQuery(id+"F0.wireOp",EDGE,"E10.0.12.5"),sQuery(id+"F0.wireOp",EDGE,"E10.0.12.6"),sQuery(id+"F0.wireOp",EDGE,"E10.0.12.9"),sQuery(id+"F0.wireOp",EDGE,"E10.0.12.10"),sQuery(id+"F0.wireOp",EDGE,"E10.0.12.11"),sQuery(id+"F0.wireOp",EDGE,"E10.0.13.2"),sQuery(id+"F0.wireOp",EDGE,"E10.0.13.3"),sQuery(id+"F0.wireOp",EDGE,"E10.0.13.4"),sQuery(id+"F0.wireOp",EDGE,"E10.0.13.5"),sQuery(id+"F0.wireOp",EDGE,"E10.0.13.6"),sQuery(id+"F0.wireOp",EDGE,"E10.0.13.9"),sQuery(id+"F0.wireOp",EDGE,"E10.0.13.10"),sQuery(id+"F0.wireOp",EDGE,"E10.0.13.11"),sQuery(id+"F0.wireOp",EDGE,"E10.0.14.2"),sQuery(id+"F0.wireOp",EDGE,"E10.0.14.3"),sQuery(id+"F0.wireOp",EDGE,"E10.0.14.4"),sQuery(id+"F0.wireOp",EDGE,"E10.0.14.5"),sQuery(id+"F0.wireOp",EDGE,"E10.0.14.6"),sQuery(id+"F0.wireOp",EDGE,"E10.0.14.9"),sQuery(id+"F0.wireOp",EDGE,"E10.0.14.10"),sQuery(id+"F0.wireOp",EDGE,"E10.0.14.11"),sQuery(id+"F0.wireOp",EDGE,"E10.0.15.2"),sQuery(id+"F0.wireOp",EDGE,"E10.0.15.3"),sQuery(id+"F0.wireOp",EDGE,"E10.0.15.4"),sQuery(id+"F0.wireOp",EDGE,"E10.0.15.5"),sQuery(id+"F0.wireOp",EDGE,"E10.0.15.6"),sQuery(id+"F0.wireOp",EDGE,"E10.0.15.9"),sQuery(id+"F0.wireOp",EDGE,"E10.0.15.10"),sQuery(id+"F0.wireOp",EDGE,"E10.0.15.11"),sQuery(id+"F0.wireOp",EDGE,"E12.bottom"),sQuery(id+"F0.wireOp",EDGE,"E12.top"),sQuery(id+"F0.wireOp",EDGE,"E12.left"),sQuery(id+"F0.wireOp",EDGE,"E12.right"),sQuery(id+"F0.wireOp",EDGE,"E13.0.1.0"),sQuery(id+"F0.wireOp",EDGE,"E13.0.1.1"),sQuery(id+"F0.wireOp",EDGE,"E13.0.1.2"),sQuery(id+"F0.wireOp",EDGE,"E13.0.1.4"),sQuery(id+"F0.wireOp",EDGE,"E13.0.2.0"),sQuery(id+"F0.wireOp",EDGE,"E13.0.2.1"),sQuery(id+"F0.wireOp",EDGE,"E13.0.2.2"),sQuery(id+"F0.wireOp",EDGE,"E13.0.2.4"),sQuery(id+"F0.wireOp",EDGE,"E13.0.3.0"),sQuery(id+"F0.wireOp",EDGE,"E13.0.3.1"),sQuery(id+"F0.wireOp",EDGE,"E13.0.3.2"),sQuery(id+"F0.wireOp",EDGE,"E13.0.3.4"),sQuery(id+"F0.wireOp",EDGE,"E13.0.4.0"),sQuery(id+"F0.wireOp",EDGE,"E13.0.4.1"),sQuery(id+"F0.wireOp",EDGE,"E13.0.4.2"),sQuery(id+"F0.wireOp",EDGE,"E13.0.4.4"),sQuery(id+"F0.wireOp",EDGE,"E13.0.5.0"),sQuery(id+"F0.wireOp",EDGE,"E13.0.5.1"),sQuery(id+"F0.wireOp",EDGE,"E13.0.5.2"),sQuery(id+"F0.wireOp",EDGE,"E13.0.5.4"),sQuery(id+"F0.wireOp",EDGE,"E13.0.6.0"),sQuery(id+"F0.wireOp",EDGE,"E13.0.6.1"),sQuery(id+"F0.wireOp",EDGE,"E13.0.6.2"),sQuery(id+"F0.wireOp",EDGE,"E13.0.6.4"),sQuery(id+"F0.wireOp",EDGE,"E13.0.7.0"),sQuery(id+"F0.wireOp",EDGE,"E13.0.7.1"),sQuery(id+"F0.wireOp",EDGE,"E13.0.7.2"),sQuery(id+"F0.wireOp",EDGE,"E13.0.7.4"),sQuery(id+"F0.wireOp",EDGE,"E13.0.8.0"),sQuery(id+"F0.wireOp",EDGE,"E13.0.8.1"),sQuery(id+"F0.wireOp",EDGE,"E13.0.8.2"),sQuery(id+"F0.wireOp",EDGE,"E13.0.8.4"),sQuery(id+"F0.wireOp",EDGE,"E13.0.9.0"),sQuery(id+"F0.wireOp",EDGE,"E13.0.9.1"),sQuery(id+"F0.wireOp",EDGE,"E13.0.9.2"),sQuery(id+"F0.wireOp",EDGE,"E13.0.9.4"),sQuery(id+"F0.wireOp",EDGE,"E13.0.10.0"),sQuery(id+"F0.wireOp",EDGE,"E13.0.10.1"),sQuery(id+"F0.wireOp",EDGE,"E13.0.10.2"),sQuery(id+"F0.wireOp",EDGE,"E13.0.10.4"),sQuery(id+"F0.wireOp",EDGE,"E13.0.11.0"),sQuery(id+"F0.wireOp",EDGE,"E13.0.11.1"),sQuery(id+"F0.wireOp",EDGE,"E13.0.11.2"),sQuery(id+"F0.wireOp",EDGE,"E13.0.11.4"),sQuery(id+"F0.wireOp",EDGE,"E13.0.12.0"),sQuery(id+"F0.wireOp",EDGE,"E13.0.12.1"),sQuery(id+"F0.wireOp",EDGE,"E13.0.12.2"),sQuery(id+"F0.wireOp",EDGE,"E13.0.12.4"),sQuery(id+"F0.wireOp",EDGE,"E13.0.13.0"),sQuery(id+"F0.wireOp",EDGE,"E13.0.13.1"),sQuery(id+"F0.wireOp",EDGE,"E13.0.13.2"),sQuery(id+"F0.wireOp",EDGE,"E13.0.13.4"),sQuery(id+"F0.wireOp",EDGE,"E13.0.14.0"),sQuery(id+"F0.wireOp",EDGE,"E13.0.14.1"),sQuery(id+"F0.wireOp",EDGE,"E13.0.14.2"),sQuery(id+"F0.wireOp",EDGE,"E13.0.14.4")])],"isStart":true});Q0=makeQuery(id+"F2.boolean.opBoolean","MERGE",FACE,{"derivedFrom":[subQ0,makeQuery(id+"F2.opPattern","COPY",FACE,{"derivedFrom":subQ0,"instanceName":"1"})]});}
            var sketch = newSketch(context, id + "F3", { "sketchPlane" : qUnion([Q0])});
            skPoint(sketch, "E14", {"position": v(-35.7, -103.68) * mm});
            skPoint(sketch, "E15", {"position": v(-35.7, -137.79) * mm});
            skPoint(sketch, "E16", {"position": v(-35.7, 65.41) * mm});
            skPoint(sketch, "E17", {"position": v(-35.7, 27.31) * mm});
            skPoint(sketch, "E18", {"position": v(-57.04, 27.31) * mm});
            skArc(sketch, "E19", {"start": v(-35.7, 65.41) * mm, "mid": v(-49.83, 48.3) * mm, "end": v(-57.04, 27.31) * mm});
            skLineSegment(sketch, "E20", {"start": v(-57.04, -36.19) * mm, "end": v(-35.7, -36.19) * mm, "construction": true});
            skPoint(sketch, "E21.MirrorP", {"position": v(-35.7, -99.69) * mm});
            skPoint(sketch, "E22.MirrorP", {"position": v(-57.04, -99.69) * mm});
            skArc(sketch, "E23.MirrorCS", {"start": v(-35.7, -137.79) * mm, "mid": v(-49.83, -120.67) * mm, "end": v(-57.04, -99.69) * mm});
            skLineSegment(sketch, "E24.bottom", {"start": v(-57.04, -99.69) * mm, "end": v(-60.85, -99.69) * mm});
            skLineSegment(sketch, "E24.top", {"start": v(-57.04, 27.31) * mm, "end": v(-60.85, 27.31) * mm});
            skLineSegment(sketch, "E24.right", {"start": v(-60.85, -99.69) * mm, "end": v(-60.85, 27.31) * mm});
            skPoint(sketch, "E25.MirrorCS.end.orphan", {"position": v(-57.04, -36.19) * mm});
            skArc(sketch, "E26", {"start": v(-60.85, 27.31) * mm, "mid": v(-114.59, -36.19) * mm, "end": v(-60.85, -99.69) * mm});
            skLineSegment(sketch, "E27", {"start": v(-57.04, -99.69) * mm, "end": v(-57.04, 27.31) * mm});
            skLineSegment(sketch, "E28", {"start": v(-35.7, -137.79) * mm, "end": v(-35.7, 65.41) * mm});
            skSolve(sketch);
        }
        {
            var Q0;
            Q0 = qSketchRegion(id + "F3", true);
            extrude(context, id + "F4", {"entities" : qUnion([Q0]), "operationType" : NewBodyOperationType.ADD, "oppositeDirection" : true, "depth" : 3.17 * mm});
        }
        {
            var Q0;
            {var subQ0=makeQuery(id+"F1.opExtrude","CAP_FACE",FACE,{"disambiguationData":[OSD([sQuery(id+"F0.wireOp",EDGE,"E0.bottom"),sQuery(id+"F0.wireOp",EDGE,"E0.top"),sQuery(id+"F0.wireOp",EDGE,"E0.left"),sQuery(id+"F0.wireOp",EDGE,"E0.right"),sQuery(id+"F0.wireOp",EDGE,"E3.bottom"),sQuery(id+"F0.wireOp",EDGE,"E3.top"),sQuery(id+"F0.wireOp",EDGE,"E3.left"),sQuery(id+"F0.wireOp",EDGE,"E3.right"),sQuery(id+"F0.wireOp",EDGE,"E8.bottom"),sQuery(id+"F0.wireOp",EDGE,"E8.top"),sQuery(id+"F0.wireOp",EDGE,"E8.left"),sQuery(id+"F0.wireOp",EDGE,"E8.right"),sQuery(id+"F0.wireOp",EDGE,"E10.0.1.2"),sQuery(id+"F0.wireOp",EDGE,"E10.0.1.3"),sQuery(id+"F0.wireOp",EDGE,"E10.0.1.4"),sQuery(id+"F0.wireOp",EDGE,"E10.0.1.5"),sQuery(id+"F0.wireOp",EDGE,"E10.0.1.6"),sQuery(id+"F0.wireOp",EDGE,"E10.0.1.9"),sQuery(id+"F0.wireOp",EDGE,"E10.0.1.10"),sQuery(id+"F0.wireOp",EDGE,"E10.0.1.11"),sQuery(id+"F0.wireOp",EDGE,"E10.0.2.2"),sQuery(id+"F0.wireOp",EDGE,"E10.0.2.3"),sQuery(id+"F0.wireOp",EDGE,"E10.0.2.4"),sQuery(id+"F0.wireOp",EDGE,"E10.0.2.5"),sQuery(id+"F0.wireOp",EDGE,"E10.0.2.6"),sQuery(id+"F0.wireOp",EDGE,"E10.0.2.9"),sQuery(id+"F0.wireOp",EDGE,"E10.0.2.10"),sQuery(id+"F0.wireOp",EDGE,"E10.0.2.11"),sQuery(id+"F0.wireOp",EDGE,"E10.0.3.2"),sQuery(id+"F0.wireOp",EDGE,"E10.0.3.3"),sQuery(id+"F0.wireOp",EDGE,"E10.0.3.4"),sQuery(id+"F0.wireOp",EDGE,"E10.0.3.5"),sQuery(id+"F0.wireOp",EDGE,"E10.0.3.6"),sQuery(id+"F0.wireOp",EDGE,"E10.0.3.9"),sQuery(id+"F0.wireOp",EDGE,"E10.0.3.10"),sQuery(id+"F0.wireOp",EDGE,"E10.0.3.11"),sQuery(id+"F0.wireOp",EDGE,"E10.0.4.2"),sQuery(id+"F0.wireOp",EDGE,"E10.0.4.3"),sQuery(id+"F0.wireOp",EDGE,"E10.0.4.4"),sQuery(id+"F0.wireOp",EDGE,"E10.0.4.5"),sQuery(id+"F0.wireOp",EDGE,"E10.0.4.6"),sQuery(id+"F0.wireOp",EDGE,"E10.0.4.9"),sQuery(id+"F0.wireOp",EDGE,"E10.0.4.10"),sQuery(id+"F0.wireOp",EDGE,"E10.0.4.11"),sQuery(id+"F0.wireOp",EDGE,"E10.0.5.2"),sQuery(id+"F0.wireOp",EDGE,"E10.0.5.3"),sQuery(id+"F0.wireOp",EDGE,"E10.0.5.4"),sQuery(id+"F0.wireOp",EDGE,"E10.0.5.5"),sQuery(id+"F0.wireOp",EDGE,"E10.0.5.6"),sQuery(id+"F0.wireOp",EDGE,"E10.0.5.9"),sQuery(id+"F0.wireOp",EDGE,"E10.0.5.10"),sQuery(id+"F0.wireOp",EDGE,"E10.0.5.11"),sQuery(id+"F0.wireOp",EDGE,"E10.0.6.2"),sQuery(id+"F0.wireOp",EDGE,"E10.0.6.3"),sQuery(id+"F0.wireOp",EDGE,"E10.0.6.4"),sQuery(id+"F0.wireOp",EDGE,"E10.0.6.5"),sQuery(id+"F0.wireOp",EDGE,"E10.0.6.6"),sQuery(id+"F0.wireOp",EDGE,"E10.0.6.9"),sQuery(id+"F0.wireOp",EDGE,"E10.0.6.10"),sQuery(id+"F0.wireOp",EDGE,"E10.0.6.11"),sQuery(id+"F0.wireOp",EDGE,"E10.0.7.2"),sQuery(id+"F0.wireOp",EDGE,"E10.0.7.3"),sQuery(id+"F0.wireOp",EDGE,"E10.0.7.4"),sQuery(id+"F0.wireOp",EDGE,"E10.0.7.5"),sQuery(id+"F0.wireOp",EDGE,"E10.0.7.6"),sQuery(id+"F0.wireOp",EDGE,"E10.0.7.9"),sQuery(id+"F0.wireOp",EDGE,"E10.0.7.10"),sQuery(id+"F0.wireOp",EDGE,"E10.0.7.11"),sQuery(id+"F0.wireOp",EDGE,"E10.0.8.2"),sQuery(id+"F0.wireOp",EDGE,"E10.0.8.3"),sQuery(id+"F0.wireOp",EDGE,"E10.0.8.4"),sQuery(id+"F0.wireOp",EDGE,"E10.0.8.5"),sQuery(id+"F0.wireOp",EDGE,"E10.0.8.6"),sQuery(id+"F0.wireOp",EDGE,"E10.0.8.9"),sQuery(id+"F0.wireOp",EDGE,"E10.0.8.10"),sQuery(id+"F0.wireOp",EDGE,"E10.0.8.11"),sQuery(id+"F0.wireOp",EDGE,"E10.0.9.2"),sQuery(id+"F0.wireOp",EDGE,"E10.0.9.3"),sQuery(id+"F0.wireOp",EDGE,"E10.0.9.4"),sQuery(id+"F0.wireOp",EDGE,"E10.0.9.5"),sQuery(id+"F0.wireOp",EDGE,"E10.0.9.6"),sQuery(id+"F0.wireOp",EDGE,"E10.0.9.9"),sQuery(id+"F0.wireOp",EDGE,"E10.0.9.10"),sQuery(id+"F0.wireOp",EDGE,"E10.0.9.11"),sQuery(id+"F0.wireOp",EDGE,"E10.0.10.2"),sQuery(id+"F0.wireOp",EDGE,"E10.0.10.3"),sQuery(id+"F0.wireOp",EDGE,"E10.0.10.4"),sQuery(id+"F0.wireOp",EDGE,"E10.0.10.5"),sQuery(id+"F0.wireOp",EDGE,"E10.0.10.6"),sQuery(id+"F0.wireOp",EDGE,"E10.0.10.9"),sQuery(id+"F0.wireOp",EDGE,"E10.0.10.10"),sQuery(id+"F0.wireOp",EDGE,"E10.0.10.11"),sQuery(id+"F0.wireOp",EDGE,"E10.0.11.2"),sQuery(id+"F0.wireOp",EDGE,"E10.0.11.3"),sQuery(id+"F0.wireOp",EDGE,"E10.0.11.4"),sQuery(id+"F0.wireOp",EDGE,"E10.0.11.5"),sQuery(id+"F0.wireOp",EDGE,"E10.0.11.6"),sQuery(id+"F0.wireOp",EDGE,"E10.0.11.9"),sQuery(id+"F0.wireOp",EDGE,"E10.0.11.10"),sQuery(id+"F0.wireOp",EDGE,"E10.0.11.11"),sQuery(id+"F0.wireOp",EDGE,"E10.0.12.2"),sQuery(id+"F0.wireOp",EDGE,"E10.0.12.3"),sQuery(id+"F0.wireOp",EDGE,"E10.0.12.4"),sQuery(id+"F0.wireOp",EDGE,"E10.0.12.5"),sQuery(id+"F0.wireOp",EDGE,"E10.0.12.6"),sQuery(id+"F0.wireOp",EDGE,"E10.0.12.9"),sQuery(id+"F0.wireOp",EDGE,"E10.0.12.10"),sQuery(id+"F0.wireOp",EDGE,"E10.0.12.11"),sQuery(id+"F0.wireOp",EDGE,"E10.0.13.2"),sQuery(id+"F0.wireOp",EDGE,"E10.0.13.3"),sQuery(id+"F0.wireOp",EDGE,"E10.0.13.4"),sQuery(id+"F0.wireOp",EDGE,"E10.0.13.5"),sQuery(id+"F0.wireOp",EDGE,"E10.0.13.6"),sQuery(id+"F0.wireOp",EDGE,"E10.0.13.9"),sQuery(id+"F0.wireOp",EDGE,"E10.0.13.10"),sQuery(id+"F0.wireOp",EDGE,"E10.0.13.11"),sQuery(id+"F0.wireOp",EDGE,"E10.0.14.2"),sQuery(id+"F0.wireOp",EDGE,"E10.0.14.3"),sQuery(id+"F0.wireOp",EDGE,"E10.0.14.4"),sQuery(id+"F0.wireOp",EDGE,"E10.0.14.5"),sQuery(id+"F0.wireOp",EDGE,"E10.0.14.6"),sQuery(id+"F0.wireOp",EDGE,"E10.0.14.9"),sQuery(id+"F0.wireOp",EDGE,"E10.0.14.10"),sQuery(id+"F0.wireOp",EDGE,"E10.0.14.11"),sQuery(id+"F0.wireOp",EDGE,"E10.0.15.2"),sQuery(id+"F0.wireOp",EDGE,"E10.0.15.3"),sQuery(id+"F0.wireOp",EDGE,"E10.0.15.4"),sQuery(id+"F0.wireOp",EDGE,"E10.0.15.5"),sQuery(id+"F0.wireOp",EDGE,"E10.0.15.6"),sQuery(id+"F0.wireOp",EDGE,"E10.0.15.9"),sQuery(id+"F0.wireOp",EDGE,"E10.0.15.10"),sQuery(id+"F0.wireOp",EDGE,"E10.0.15.11"),sQuery(id+"F0.wireOp",EDGE,"E12.bottom"),sQuery(id+"F0.wireOp",EDGE,"E12.top"),sQuery(id+"F0.wireOp",EDGE,"E12.left"),sQuery(id+"F0.wireOp",EDGE,"E12.right"),sQuery(id+"F0.wireOp",EDGE,"E13.0.1.0"),sQuery(id+"F0.wireOp",EDGE,"E13.0.1.1"),sQuery(id+"F0.wireOp",EDGE,"E13.0.1.2"),sQuery(id+"F0.wireOp",EDGE,"E13.0.1.4"),sQuery(id+"F0.wireOp",EDGE,"E13.0.2.0"),sQuery(id+"F0.wireOp",EDGE,"E13.0.2.1"),sQuery(id+"F0.wireOp",EDGE,"E13.0.2.2"),sQuery(id+"F0.wireOp",EDGE,"E13.0.2.4"),sQuery(id+"F0.wireOp",EDGE,"E13.0.3.0"),sQuery(id+"F0.wireOp",EDGE,"E13.0.3.1"),sQuery(id+"F0.wireOp",EDGE,"E13.0.3.2"),sQuery(id+"F0.wireOp",EDGE,"E13.0.3.4"),sQuery(id+"F0.wireOp",EDGE,"E13.0.4.0"),sQuery(id+"F0.wireOp",EDGE,"E13.0.4.1"),sQuery(id+"F0.wireOp",EDGE,"E13.0.4.2"),sQuery(id+"F0.wireOp",EDGE,"E13.0.4.4"),sQuery(id+"F0.wireOp",EDGE,"E13.0.5.0"),sQuery(id+"F0.wireOp",EDGE,"E13.0.5.1"),sQuery(id+"F0.wireOp",EDGE,"E13.0.5.2"),sQuery(id+"F0.wireOp",EDGE,"E13.0.5.4"),sQuery(id+"F0.wireOp",EDGE,"E13.0.6.0"),sQuery(id+"F0.wireOp",EDGE,"E13.0.6.1"),sQuery(id+"F0.wireOp",EDGE,"E13.0.6.2"),sQuery(id+"F0.wireOp",EDGE,"E13.0.6.4"),sQuery(id+"F0.wireOp",EDGE,"E13.0.7.0"),sQuery(id+"F0.wireOp",EDGE,"E13.0.7.1"),sQuery(id+"F0.wireOp",EDGE,"E13.0.7.2"),sQuery(id+"F0.wireOp",EDGE,"E13.0.7.4"),sQuery(id+"F0.wireOp",EDGE,"E13.0.8.0"),sQuery(id+"F0.wireOp",EDGE,"E13.0.8.1"),sQuery(id+"F0.wireOp",EDGE,"E13.0.8.2"),sQuery(id+"F0.wireOp",EDGE,"E13.0.8.4"),sQuery(id+"F0.wireOp",EDGE,"E13.0.9.0"),sQuery(id+"F0.wireOp",EDGE,"E13.0.9.1"),sQuery(id+"F0.wireOp",EDGE,"E13.0.9.2"),sQuery(id+"F0.wireOp",EDGE,"E13.0.9.4"),sQuery(id+"F0.wireOp",EDGE,"E13.0.10.0"),sQuery(id+"F0.wireOp",EDGE,"E13.0.10.1"),sQuery(id+"F0.wireOp",EDGE,"E13.0.10.2"),sQuery(id+"F0.wireOp",EDGE,"E13.0.10.4"),sQuery(id+"F0.wireOp",EDGE,"E13.0.11.0"),sQuery(id+"F0.wireOp",EDGE,"E13.0.11.1"),sQuery(id+"F0.wireOp",EDGE,"E13.0.11.2"),sQuery(id+"F0.wireOp",EDGE,"E13.0.11.4"),sQuery(id+"F0.wireOp",EDGE,"E13.0.12.0"),sQuery(id+"F0.wireOp",EDGE,"E13.0.12.1"),sQuery(id+"F0.wireOp",EDGE,"E13.0.12.2"),sQuery(id+"F0.wireOp",EDGE,"E13.0.12.4"),sQuery(id+"F0.wireOp",EDGE,"E13.0.13.0"),sQuery(id+"F0.wireOp",EDGE,"E13.0.13.1"),sQuery(id+"F0.wireOp",EDGE,"E13.0.13.2"),sQuery(id+"F0.wireOp",EDGE,"E13.0.13.4"),sQuery(id+"F0.wireOp",EDGE,"E13.0.14.0"),sQuery(id+"F0.wireOp",EDGE,"E13.0.14.1"),sQuery(id+"F0.wireOp",EDGE,"E13.0.14.2"),sQuery(id+"F0.wireOp",EDGE,"E13.0.14.4")])],"isStart":false});Q0=makeQuery(id+"F4.boolean.opBoolean","MERGE",FACE,{"derivedFrom":[makeQuery(id+"F2.boolean.opBoolean","MERGE",FACE,{"derivedFrom":[subQ0,makeQuery(id+"F2.opPattern","COPY",FACE,{"derivedFrom":subQ0,"instanceName":"1"})]}),makeQuery(id+"F4.opExtrude","CAP_FACE",FACE,{"disambiguationData":[OSD([sQuery(id+"F3.wireOp",EDGE,"E19"),sQuery(id+"F3.wireOp",EDGE,"E23.MirrorCS"),sQuery(id+"F3.wireOp",EDGE,"E24.bottom"),sQuery(id+"F3.wireOp",EDGE,"E24.top"),sQuery(id+"F3.wireOp",EDGE,"E26"),sQuery(id+"F3.wireOp",EDGE,"E28")])],"isStart":false})]});}
            var sketch = newSketch(context, id + "F5", { "sketchPlane" : qUnion([Q0])});
            skLineSegment(sketch, "E29.bottom", {"start": v(-35.7, -65.41) * mm, "end": v(-11.58, -65.41) * mm});
            skLineSegment(sketch, "E29.top", {"start": v(-35.7, 137.79) * mm, "end": v(-11.58, 137.79) * mm});
            skLineSegment(sketch, "E29.left", {"start": v(-35.7, -65.41) * mm, "end": v(-35.7, 137.79) * mm});
            skLineSegment(sketch, "E29.right", {"start": v(-11.58, -65.41) * mm, "end": v(-11.58, 137.79) * mm});
            skSolve(sketch);
        }
        {
            var Q0;
            Q0 = qSketchRegion(id + "F5", true);
            extrude(context, id + "F6", {"entities" : qUnion([Q0]), "operationType" : NewBodyOperationType.ADD, "oppositeDirection" : true, "depth" : 3.17 * mm});
        }
        {
            var Q0;
            {var subQ0=makeQuery(id+"F1.opExtrude","CAP_FACE",FACE,{"disambiguationData":[OSD([sQuery(id+"F0.wireOp",EDGE,"E0.bottom"),sQuery(id+"F0.wireOp",EDGE,"E0.top"),sQuery(id+"F0.wireOp",EDGE,"E0.left"),sQuery(id+"F0.wireOp",EDGE,"E0.right"),sQuery(id+"F0.wireOp",EDGE,"E3.bottom"),sQuery(id+"F0.wireOp",EDGE,"E3.top"),sQuery(id+"F0.wireOp",EDGE,"E3.left"),sQuery(id+"F0.wireOp",EDGE,"E3.right"),sQuery(id+"F0.wireOp",EDGE,"E8.bottom"),sQuery(id+"F0.wireOp",EDGE,"E8.top"),sQuery(id+"F0.wireOp",EDGE,"E8.left"),sQuery(id+"F0.wireOp",EDGE,"E8.right"),sQuery(id+"F0.wireOp",EDGE,"E10.0.1.2"),sQuery(id+"F0.wireOp",EDGE,"E10.0.1.3"),sQuery(id+"F0.wireOp",EDGE,"E10.0.1.4"),sQuery(id+"F0.wireOp",EDGE,"E10.0.1.5"),sQuery(id+"F0.wireOp",EDGE,"E10.0.1.6"),sQuery(id+"F0.wireOp",EDGE,"E10.0.1.9"),sQuery(id+"F0.wireOp",EDGE,"E10.0.1.10"),sQuery(id+"F0.wireOp",EDGE,"E10.0.1.11"),sQuery(id+"F0.wireOp",EDGE,"E10.0.2.2"),sQuery(id+"F0.wireOp",EDGE,"E10.0.2.3"),sQuery(id+"F0.wireOp",EDGE,"E10.0.2.4"),sQuery(id+"F0.wireOp",EDGE,"E10.0.2.5"),sQuery(id+"F0.wireOp",EDGE,"E10.0.2.6"),sQuery(id+"F0.wireOp",EDGE,"E10.0.2.9"),sQuery(id+"F0.wireOp",EDGE,"E10.0.2.10"),sQuery(id+"F0.wireOp",EDGE,"E10.0.2.11"),sQuery(id+"F0.wireOp",EDGE,"E10.0.3.2"),sQuery(id+"F0.wireOp",EDGE,"E10.0.3.3"),sQuery(id+"F0.wireOp",EDGE,"E10.0.3.4"),sQuery(id+"F0.wireOp",EDGE,"E10.0.3.5"),sQuery(id+"F0.wireOp",EDGE,"E10.0.3.6"),sQuery(id+"F0.wireOp",EDGE,"E10.0.3.9"),sQuery(id+"F0.wireOp",EDGE,"E10.0.3.10"),sQuery(id+"F0.wireOp",EDGE,"E10.0.3.11"),sQuery(id+"F0.wireOp",EDGE,"E10.0.4.2"),sQuery(id+"F0.wireOp",EDGE,"E10.0.4.3"),sQuery(id+"F0.wireOp",EDGE,"E10.0.4.4"),sQuery(id+"F0.wireOp",EDGE,"E10.0.4.5"),sQuery(id+"F0.wireOp",EDGE,"E10.0.4.6"),sQuery(id+"F0.wireOp",EDGE,"E10.0.4.9"),sQuery(id+"F0.wireOp",EDGE,"E10.0.4.10"),sQuery(id+"F0.wireOp",EDGE,"E10.0.4.11"),sQuery(id+"F0.wireOp",EDGE,"E10.0.5.2"),sQuery(id+"F0.wireOp",EDGE,"E10.0.5.3"),sQuery(id+"F0.wireOp",EDGE,"E10.0.5.4"),sQuery(id+"F0.wireOp",EDGE,"E10.0.5.5"),sQuery(id+"F0.wireOp",EDGE,"E10.0.5.6"),sQuery(id+"F0.wireOp",EDGE,"E10.0.5.9"),sQuery(id+"F0.wireOp",EDGE,"E10.0.5.10"),sQuery(id+"F0.wireOp",EDGE,"E10.0.5.11"),sQuery(id+"F0.wireOp",EDGE,"E10.0.6.2"),sQuery(id+"F0.wireOp",EDGE,"E10.0.6.3"),sQuery(id+"F0.wireOp",EDGE,"E10.0.6.4"),sQuery(id+"F0.wireOp",EDGE,"E10.0.6.5"),sQuery(id+"F0.wireOp",EDGE,"E10.0.6.6"),sQuery(id+"F0.wireOp",EDGE,"E10.0.6.9"),sQuery(id+"F0.wireOp",EDGE,"E10.0.6.10"),sQuery(id+"F0.wireOp",EDGE,"E10.0.6.11"),sQuery(id+"F0.wireOp",EDGE,"E10.0.7.2"),sQuery(id+"F0.wireOp",EDGE,"E10.0.7.3"),sQuery(id+"F0.wireOp",EDGE,"E10.0.7.4"),sQuery(id+"F0.wireOp",EDGE,"E10.0.7.5"),sQuery(id+"F0.wireOp",EDGE,"E10.0.7.6"),sQuery(id+"F0.wireOp",EDGE,"E10.0.7.9"),sQuery(id+"F0.wireOp",EDGE,"E10.0.7.10"),sQuery(id+"F0.wireOp",EDGE,"E10.0.7.11"),sQuery(id+"F0.wireOp",EDGE,"E10.0.8.2"),sQuery(id+"F0.wireOp",EDGE,"E10.0.8.3"),sQuery(id+"F0.wireOp",EDGE,"E10.0.8.4"),sQuery(id+"F0.wireOp",EDGE,"E10.0.8.5"),sQuery(id+"F0.wireOp",EDGE,"E10.0.8.6"),sQuery(id+"F0.wireOp",EDGE,"E10.0.8.9"),sQuery(id+"F0.wireOp",EDGE,"E10.0.8.10"),sQuery(id+"F0.wireOp",EDGE,"E10.0.8.11"),sQuery(id+"F0.wireOp",EDGE,"E10.0.9.2"),sQuery(id+"F0.wireOp",EDGE,"E10.0.9.3"),sQuery(id+"F0.wireOp",EDGE,"E10.0.9.4"),sQuery(id+"F0.wireOp",EDGE,"E10.0.9.5"),sQuery(id+"F0.wireOp",EDGE,"E10.0.9.6"),sQuery(id+"F0.wireOp",EDGE,"E10.0.9.9"),sQuery(id+"F0.wireOp",EDGE,"E10.0.9.10"),sQuery(id+"F0.wireOp",EDGE,"E10.0.9.11"),sQuery(id+"F0.wireOp",EDGE,"E10.0.10.2"),sQuery(id+"F0.wireOp",EDGE,"E10.0.10.3"),sQuery(id+"F0.wireOp",EDGE,"E10.0.10.4"),sQuery(id+"F0.wireOp",EDGE,"E10.0.10.5"),sQuery(id+"F0.wireOp",EDGE,"E10.0.10.6"),sQuery(id+"F0.wireOp",EDGE,"E10.0.10.9"),sQuery(id+"F0.wireOp",EDGE,"E10.0.10.10"),sQuery(id+"F0.wireOp",EDGE,"E10.0.10.11"),sQuery(id+"F0.wireOp",EDGE,"E10.0.11.2"),sQuery(id+"F0.wireOp",EDGE,"E10.0.11.3"),sQuery(id+"F0.wireOp",EDGE,"E10.0.11.4"),sQuery(id+"F0.wireOp",EDGE,"E10.0.11.5"),sQuery(id+"F0.wireOp",EDGE,"E10.0.11.6"),sQuery(id+"F0.wireOp",EDGE,"E10.0.11.9"),sQuery(id+"F0.wireOp",EDGE,"E10.0.11.10"),sQuery(id+"F0.wireOp",EDGE,"E10.0.11.11"),sQuery(id+"F0.wireOp",EDGE,"E10.0.12.2"),sQuery(id+"F0.wireOp",EDGE,"E10.0.12.3"),sQuery(id+"F0.wireOp",EDGE,"E10.0.12.4"),sQuery(id+"F0.wireOp",EDGE,"E10.0.12.5"),sQuery(id+"F0.wireOp",EDGE,"E10.0.12.6"),sQuery(id+"F0.wireOp",EDGE,"E10.0.12.9"),sQuery(id+"F0.wireOp",EDGE,"E10.0.12.10"),sQuery(id+"F0.wireOp",EDGE,"E10.0.12.11"),sQuery(id+"F0.wireOp",EDGE,"E10.0.13.2"),sQuery(id+"F0.wireOp",EDGE,"E10.0.13.3"),sQuery(id+"F0.wireOp",EDGE,"E10.0.13.4"),sQuery(id+"F0.wireOp",EDGE,"E10.0.13.5"),sQuery(id+"F0.wireOp",EDGE,"E10.0.13.6"),sQuery(id+"F0.wireOp",EDGE,"E10.0.13.9"),sQuery(id+"F0.wireOp",EDGE,"E10.0.13.10"),sQuery(id+"F0.wireOp",EDGE,"E10.0.13.11"),sQuery(id+"F0.wireOp",EDGE,"E10.0.14.2"),sQuery(id+"F0.wireOp",EDGE,"E10.0.14.3"),sQuery(id+"F0.wireOp",EDGE,"E10.0.14.4"),sQuery(id+"F0.wireOp",EDGE,"E10.0.14.5"),sQuery(id+"F0.wireOp",EDGE,"E10.0.14.6"),sQuery(id+"F0.wireOp",EDGE,"E10.0.14.9"),sQuery(id+"F0.wireOp",EDGE,"E10.0.14.10"),sQuery(id+"F0.wireOp",EDGE,"E10.0.14.11"),sQuery(id+"F0.wireOp",EDGE,"E10.0.15.2"),sQuery(id+"F0.wireOp",EDGE,"E10.0.15.3"),sQuery(id+"F0.wireOp",EDGE,"E10.0.15.4"),sQuery(id+"F0.wireOp",EDGE,"E10.0.15.5"),sQuery(id+"F0.wireOp",EDGE,"E10.0.15.6"),sQuery(id+"F0.wireOp",EDGE,"E10.0.15.9"),sQuery(id+"F0.wireOp",EDGE,"E10.0.15.10"),sQuery(id+"F0.wireOp",EDGE,"E10.0.15.11"),sQuery(id+"F0.wireOp",EDGE,"E12.bottom"),sQuery(id+"F0.wireOp",EDGE,"E12.top"),sQuery(id+"F0.wireOp",EDGE,"E12.left"),sQuery(id+"F0.wireOp",EDGE,"E12.right"),sQuery(id+"F0.wireOp",EDGE,"E13.0.1.0"),sQuery(id+"F0.wireOp",EDGE,"E13.0.1.1"),sQuery(id+"F0.wireOp",EDGE,"E13.0.1.2"),sQuery(id+"F0.wireOp",EDGE,"E13.0.1.4"),sQuery(id+"F0.wireOp",EDGE,"E13.0.2.0"),sQuery(id+"F0.wireOp",EDGE,"E13.0.2.1"),sQuery(id+"F0.wireOp",EDGE,"E13.0.2.2"),sQuery(id+"F0.wireOp",EDGE,"E13.0.2.4"),sQuery(id+"F0.wireOp",EDGE,"E13.0.3.0"),sQuery(id+"F0.wireOp",EDGE,"E13.0.3.1"),sQuery(id+"F0.wireOp",EDGE,"E13.0.3.2"),sQuery(id+"F0.wireOp",EDGE,"E13.0.3.4"),sQuery(id+"F0.wireOp",EDGE,"E13.0.4.0"),sQuery(id+"F0.wireOp",EDGE,"E13.0.4.1"),sQuery(id+"F0.wireOp",EDGE,"E13.0.4.2"),sQuery(id+"F0.wireOp",EDGE,"E13.0.4.4"),sQuery(id+"F0.wireOp",EDGE,"E13.0.5.0"),sQuery(id+"F0.wireOp",EDGE,"E13.0.5.1"),sQuery(id+"F0.wireOp",EDGE,"E13.0.5.2"),sQuery(id+"F0.wireOp",EDGE,"E13.0.5.4"),sQuery(id+"F0.wireOp",EDGE,"E13.0.6.0"),sQuery(id+"F0.wireOp",EDGE,"E13.0.6.1"),sQuery(id+"F0.wireOp",EDGE,"E13.0.6.2"),sQuery(id+"F0.wireOp",EDGE,"E13.0.6.4"),sQuery(id+"F0.wireOp",EDGE,"E13.0.7.0"),sQuery(id+"F0.wireOp",EDGE,"E13.0.7.1"),sQuery(id+"F0.wireOp",EDGE,"E13.0.7.2"),sQuery(id+"F0.wireOp",EDGE,"E13.0.7.4"),sQuery(id+"F0.wireOp",EDGE,"E13.0.8.0"),sQuery(id+"F0.wireOp",EDGE,"E13.0.8.1"),sQuery(id+"F0.wireOp",EDGE,"E13.0.8.2"),sQuery(id+"F0.wireOp",EDGE,"E13.0.8.4"),sQuery(id+"F0.wireOp",EDGE,"E13.0.9.0"),sQuery(id+"F0.wireOp",EDGE,"E13.0.9.1"),sQuery(id+"F0.wireOp",EDGE,"E13.0.9.2"),sQuery(id+"F0.wireOp",EDGE,"E13.0.9.4"),sQuery(id+"F0.wireOp",EDGE,"E13.0.10.0"),sQuery(id+"F0.wireOp",EDGE,"E13.0.10.1"),sQuery(id+"F0.wireOp",EDGE,"E13.0.10.2"),sQuery(id+"F0.wireOp",EDGE,"E13.0.10.4"),sQuery(id+"F0.wireOp",EDGE,"E13.0.11.0"),sQuery(id+"F0.wireOp",EDGE,"E13.0.11.1"),sQuery(id+"F0.wireOp",EDGE,"E13.0.11.2"),sQuery(id+"F0.wireOp",EDGE,"E13.0.11.4"),sQuery(id+"F0.wireOp",EDGE,"E13.0.12.0"),sQuery(id+"F0.wireOp",EDGE,"E13.0.12.1"),sQuery(id+"F0.wireOp",EDGE,"E13.0.12.2"),sQuery(id+"F0.wireOp",EDGE,"E13.0.12.4"),sQuery(id+"F0.wireOp",EDGE,"E13.0.13.0"),sQuery(id+"F0.wireOp",EDGE,"E13.0.13.1"),sQuery(id+"F0.wireOp",EDGE,"E13.0.13.2"),sQuery(id+"F0.wireOp",EDGE,"E13.0.13.4"),sQuery(id+"F0.wireOp",EDGE,"E13.0.14.0"),sQuery(id+"F0.wireOp",EDGE,"E13.0.14.1"),sQuery(id+"F0.wireOp",EDGE,"E13.0.14.2"),sQuery(id+"F0.wireOp",EDGE,"E13.0.14.4")])],"isStart":false});Q0=makeQuery(id+"F6.boolean.opBoolean","MERGE",FACE,{"derivedFrom":[makeQuery(id+"F4.boolean.opBoolean","MERGE",FACE,{"derivedFrom":[makeQuery(id+"F2.boolean.opBoolean","MERGE",FACE,{"derivedFrom":[subQ0,makeQuery(id+"F2.opPattern","COPY",FACE,{"derivedFrom":subQ0,"instanceName":"1"})]}),makeQuery(id+"F4.opExtrude","CAP_FACE",FACE,{"disambiguationData":[OSD([sQuery(id+"F3.wireOp",EDGE,"E19"),sQuery(id+"F3.wireOp",EDGE,"E23.MirrorCS"),sQuery(id+"F3.wireOp",EDGE,"E24.bottom"),sQuery(id+"F3.wireOp",EDGE,"E24.top"),sQuery(id+"F3.wireOp",EDGE,"E26"),sQuery(id+"F3.wireOp",EDGE,"E28")])],"isStart":false})]}),makeQuery(id+"F6.opExtrude","CAP_FACE",FACE,{"disambiguationData":[OSD([sQuery(id+"F5.wireOp",EDGE,"E29.bottom"),sQuery(id+"F5.wireOp",EDGE,"E29.top"),sQuery(id+"F5.wireOp",EDGE,"E29.left"),sQuery(id+"F5.wireOp",EDGE,"E29.right")])],"isStart":true})]});}
            var sketch = newSketch(context, id + "F7", { "sketchPlane" : qUnion([Q0])});
            skCircle(sketch, "E30", {"center": v(-38.73, -41.32) * mm, "radius": 7.76 * mm});
            skCircle(sketch, "E31.0.1.0", {"center": v(-38.73, -15.92) * mm, "radius": 7.76 * mm});
            skCircle(sketch, "E31.0.2.0", {"center": v(-38.73, 9.48) * mm, "radius": 7.76 * mm});
            skCircle(sketch, "E31.0.3.0", {"center": v(-38.73, 34.88) * mm, "radius": 7.76 * mm});
            skCircle(sketch, "E31.0.4.0", {"center": v(-38.73, 60.28) * mm, "radius": 7.76 * mm});
            skCircle(sketch, "E31.0.5.0", {"center": v(-38.73, 85.68) * mm, "radius": 7.76 * mm});
            skCircle(sketch, "E31.0.6.0", {"center": v(-38.73, 111.08) * mm, "radius": 7.76 * mm});
            skLineSegment(sketch, "E31.direction1", {"start": v(-38.73, -41.32) * mm, "end": v(-13.33, -41.32) * mm, "construction": true});
            skLineSegment(sketch, "E31.direction2", {"start": v(-38.73, -41.32) * mm, "end": v(-38.73, -15.92) * mm, "construction": true});
            skSolve(sketch);
        }
        {
            var Q0;
            Q0=makeQuery(id+"F7.imprint","IMPRINT",FACE,{"disambiguationData":[TD([[makeQuery(id+"F7.imprint","IMPRINT",EDGE,{"derivedFrom":sQuery(id+"F7.wireOp",EDGE,"E30")}),-1.0]])]});
            var sketch = newSketch(context, id + "F8", { "sketchPlane" : qUnion([Q0])});
            skSolve(sketch);
        }
        {
            var Q0;
            Q0 = qSketchRegion(id + "F8", true);
            var Q1;
            Q1=makeQuery(id+"F1.opExtrude","SWEPT_FACE",FACE,{"disambiguationData":[OSD([sQuery(id+"F0.wireOp",EDGE,"E0.right")])]});
            extrude(context, id + "F9", {"entities" : qUnion([Q0, Q1]), "operationType" : NewBodyOperationType.REMOVE, "oppositeDirection" : true, "depth" : 0.03 * mm});
        }
    });
